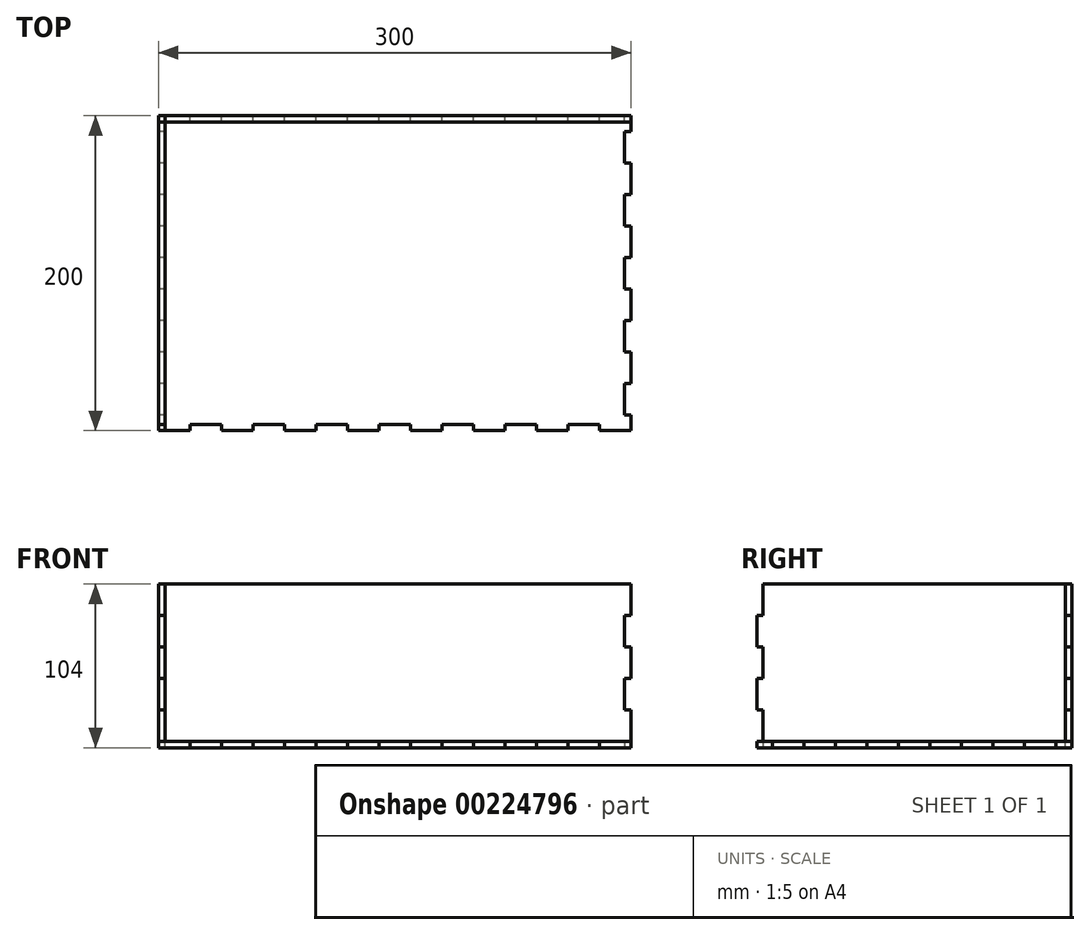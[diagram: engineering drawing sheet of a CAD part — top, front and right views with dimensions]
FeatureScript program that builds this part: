
annotation { "Feature Type Name" : "Feature", "Feature Type Description" : "" }
export const myFeature = defineFeature(function(context is Context, id is Id, definition is map)
    precondition{}
    {
        {
            var Q0;
            Q0=qCreatedBy(makeId("Top.planeOp"),FACE);
            var sketch = newSketch(context, id + "F0", { "sketchPlane" : qUnion([Q0])});
            skLineSegment(sketch, "E0.bottom", {"start": v(150, 100) * mm, "end": v(130, 100) * mm});
            skLineSegment(sketch, "E0.top", {"start": v(150, -100) * mm, "end": v(130, -100) * mm});
            skLineSegment(sketch, "E0.left", {"start": v(150, 100) * mm, "end": v(150, 90) * mm});
            skLineSegment(sketch, "E0.right", {"start": v(-150, 100) * mm, "end": v(-150, 90) * mm});
            skPoint(sketch, "E0.middle", {"position": v(0, 0) * mm});
            skPoint(sketch, "E1.endSnap0", {"position": v(0, 100) * mm});
            skLineSegment(sketch, "E2", {"start": v(0, 96) * mm, "end": v(10, 96) * mm});
            skLineSegment(sketch, "E3", {"start": v(10, 96) * mm, "end": v(10, 100) * mm});
            skLineSegment(sketch, "E4.MirrorCS", {"start": v(-10, 96) * mm, "end": v(-10, 100) * mm});
            skLineSegment(sketch, "E5.MirrorCS", {"start": v(0, 96) * mm, "end": v(-10, 96) * mm});
            skPoint(sketch, "E1.start.orphan", {"position": v(0, 100) * mm});
            skLineSegment(sketch, "E6.1.0.0", {"start": v(30, 96) * mm, "end": v(30, 100) * mm});
            skLineSegment(sketch, "E6.1.0.1", {"start": v(40, 96) * mm, "end": v(30, 96) * mm});
            skLineSegment(sketch, "E6.1.0.2", {"start": v(40, 96) * mm, "end": v(50, 96) * mm});
            skLineSegment(sketch, "E6.1.0.3", {"start": v(50, 96) * mm, "end": v(50, 100) * mm});
            skLineSegment(sketch, "E6.2.0.0", {"start": v(70, 96) * mm, "end": v(70, 100) * mm});
            skLineSegment(sketch, "E6.2.0.1", {"start": v(80, 96) * mm, "end": v(70, 96) * mm});
            skLineSegment(sketch, "E6.2.0.2", {"start": v(80, 96) * mm, "end": v(90, 96) * mm});
            skLineSegment(sketch, "E6.2.0.3", {"start": v(90, 96) * mm, "end": v(90, 100) * mm});
            skLineSegment(sketch, "E6.3.0.0", {"start": v(110, 96) * mm, "end": v(110, 100) * mm});
            skLineSegment(sketch, "E6.3.0.1", {"start": v(120, 96) * mm, "end": v(110, 96) * mm});
            skLineSegment(sketch, "E6.3.0.2", {"start": v(120, 96) * mm, "end": v(130, 96) * mm});
            skLineSegment(sketch, "E6.3.0.3", {"start": v(130, 96) * mm, "end": v(130, 100) * mm});
            skLineSegment(sketch, "E6.direction1", {"start": v(-10, 96) * mm, "end": v(30, 96) * mm, "construction": true});
            skLineSegment(sketch, "E7.MirrorCS", {"start": v(-110, 96) * mm, "end": v(-110, 100) * mm});
            skLineSegment(sketch, "E8.MirrorCS", {"start": v(-70, 96) * mm, "end": v(-70, 100) * mm});
            skLineSegment(sketch, "E9.MirrorCS", {"start": v(-50, 96) * mm, "end": v(-50, 100) * mm});
            skLineSegment(sketch, "E10.MirrorCS", {"start": v(-30, 96) * mm, "end": v(-30, 100) * mm});
            skLineSegment(sketch, "E11.MirrorCS", {"start": v(-90, 96) * mm, "end": v(-90, 100) * mm});
            skLineSegment(sketch, "E12.MirrorCS", {"start": v(-130, 96) * mm, "end": v(-130, 100) * mm});
            skLineSegment(sketch, "E13.MirrorCS", {"start": v(-120, 96) * mm, "end": v(-130, 96) * mm});
            skLineSegment(sketch, "E14.MirrorCS", {"start": v(10, 96) * mm, "end": v(-30, 96) * mm, "construction": true});
            skLineSegment(sketch, "E15.MirrorCS", {"start": v(-40, 96) * mm, "end": v(-50, 96) * mm});
            skLineSegment(sketch, "E16.MirrorCS", {"start": v(-40, 96) * mm, "end": v(-30, 96) * mm});
            skLineSegment(sketch, "E17.MirrorCS", {"start": v(-80, 96) * mm, "end": v(-90, 96) * mm});
            skLineSegment(sketch, "E18.MirrorCS", {"start": v(-120, 96) * mm, "end": v(-110, 96) * mm});
            skLineSegment(sketch, "E19.MirrorCS", {"start": v(-80, 96) * mm, "end": v(-70, 96) * mm});
            skPoint(sketch, "E20.MirrorP", {"position": v(0, -100) * mm});
            skLineSegment(sketch, "E21.MirrorCS", {"start": v(-10, -96) * mm, "end": v(-10, -100) * mm});
            skLineSegment(sketch, "E22.MirrorCS", {"start": v(10, -96) * mm, "end": v(10, -100) * mm});
            skLineSegment(sketch, "E23.MirrorCS", {"start": v(0, -96) * mm, "end": v(10, -96) * mm});
            skLineSegment(sketch, "E24.MirrorCS", {"start": v(0, -96) * mm, "end": v(-10, -96) * mm});
            skLineSegment(sketch, "E25.MirrorCS", {"start": v(-70, -96) * mm, "end": v(-70, -100) * mm});
            skLineSegment(sketch, "E26.MirrorCS", {"start": v(-130, -96) * mm, "end": v(-130, -100) * mm});
            skLineSegment(sketch, "E27.MirrorCS", {"start": v(-110, -96) * mm, "end": v(-110, -100) * mm});
            skLineSegment(sketch, "E28.MirrorCS", {"start": v(-30, -96) * mm, "end": v(-30, -100) * mm});
            skLineSegment(sketch, "E29.MirrorCS", {"start": v(110, -96) * mm, "end": v(110, -100) * mm});
            skLineSegment(sketch, "E30.MirrorCS", {"start": v(30, -96) * mm, "end": v(30, -100) * mm});
            skLineSegment(sketch, "E31.MirrorCS", {"start": v(130, -96) * mm, "end": v(130, -100) * mm});
            skLineSegment(sketch, "E32.MirrorCS", {"start": v(-50, -96) * mm, "end": v(-50, -100) * mm});
            skLineSegment(sketch, "E33.MirrorCS", {"start": v(90, -96) * mm, "end": v(90, -100) * mm});
            skLineSegment(sketch, "E34.MirrorCS", {"start": v(-90, -96) * mm, "end": v(-90, -100) * mm});
            skLineSegment(sketch, "E35.MirrorCS", {"start": v(70, -96) * mm, "end": v(70, -100) * mm});
            skLineSegment(sketch, "E36.MirrorCS", {"start": v(50, -96) * mm, "end": v(50, -100) * mm});
            skLineSegment(sketch, "E37.MirrorCS", {"start": v(-40, -96) * mm, "end": v(-30, -96) * mm});
            skLineSegment(sketch, "E38.MirrorCS", {"start": v(120, -96) * mm, "end": v(130, -96) * mm});
            skLineSegment(sketch, "E39.MirrorCS", {"start": v(-120, -96) * mm, "end": v(-130, -96) * mm});
            skLineSegment(sketch, "E40.MirrorCS", {"start": v(-40, -96) * mm, "end": v(-50, -96) * mm});
            skLineSegment(sketch, "E41.MirrorCS", {"start": v(120, -96) * mm, "end": v(110, -96) * mm});
            skLineSegment(sketch, "E42.MirrorCS", {"start": v(-80, -96) * mm, "end": v(-70, -96) * mm});
            skLineSegment(sketch, "E43.MirrorCS", {"start": v(10, -96) * mm, "end": v(-30, -96) * mm, "construction": true});
            skLineSegment(sketch, "E44.MirrorCS", {"start": v(40, -96) * mm, "end": v(50, -96) * mm});
            skLineSegment(sketch, "E45.MirrorCS", {"start": v(40, -96) * mm, "end": v(30, -96) * mm});
            skLineSegment(sketch, "E46.MirrorCS", {"start": v(-80, -96) * mm, "end": v(-90, -96) * mm});
            skLineSegment(sketch, "E47.MirrorCS", {"start": v(-120, -96) * mm, "end": v(-110, -96) * mm});
            skLineSegment(sketch, "E48.MirrorCS", {"start": v(80, -96) * mm, "end": v(90, -96) * mm});
            skLineSegment(sketch, "E49.MirrorCS", {"start": v(80, -96) * mm, "end": v(70, -96) * mm});
            skLineSegment(sketch, "E50.MirrorCS", {"start": v(-10, -96) * mm, "end": v(30, -96) * mm, "construction": true});
            skPoint(sketch, "E51.endSnap0", {"position": v(-150, 0) * mm});
            skLineSegment(sketch, "E52", {"start": v(-146, 0) * mm, "end": v(-146, 10) * mm});
            skLineSegment(sketch, "E53", {"start": v(-146, 10) * mm, "end": v(-150, 10) * mm});
            skLineSegment(sketch, "E54.MirrorCS", {"start": v(-146, 0) * mm, "end": v(-146, -10) * mm});
            skLineSegment(sketch, "E55.MirrorCS", {"start": v(-146, -10) * mm, "end": v(-150, -10) * mm});
            skPoint(sketch, "E51.start.orphan", {"position": v(-150, 0) * mm});
            skLineSegment(sketch, "E56.0.1.0", {"start": v(-146, 30) * mm, "end": v(-150, 30) * mm});
            skLineSegment(sketch, "E56.0.1.1", {"start": v(-146, 40) * mm, "end": v(-146, 30) * mm});
            skLineSegment(sketch, "E56.0.1.2", {"start": v(-146, 40) * mm, "end": v(-146, 50) * mm});
            skLineSegment(sketch, "E56.0.1.3", {"start": v(-146, 50) * mm, "end": v(-150, 50) * mm});
            skLineSegment(sketch, "E56.0.2.0", {"start": v(-146, 70) * mm, "end": v(-150, 70) * mm});
            skLineSegment(sketch, "E56.0.2.1", {"start": v(-146, 80) * mm, "end": v(-146, 70) * mm});
            skLineSegment(sketch, "E56.0.2.2", {"start": v(-146, 80) * mm, "end": v(-146, 90) * mm});
            skLineSegment(sketch, "E56.0.2.3", {"start": v(-146, 90) * mm, "end": v(-150, 90) * mm});
            skLineSegment(sketch, "E56.direction1", {"start": v(-150, -10) * mm, "end": v(-125, -10) * mm, "construction": true});
            skLineSegment(sketch, "E56.direction2", {"start": v(-150, 10) * mm, "end": v(-150, 30) * mm, "construction": true});
            skLineSegment(sketch, "E57.MirrorCS", {"start": v(-146, -30) * mm, "end": v(-150, -30) * mm});
            skLineSegment(sketch, "E58.MirrorCS", {"start": v(-146, -90) * mm, "end": v(-150, -90) * mm});
            skLineSegment(sketch, "E59.MirrorCS", {"start": v(-146, -70) * mm, "end": v(-150, -70) * mm});
            skLineSegment(sketch, "E60.MirrorCS", {"start": v(-146, -50) * mm, "end": v(-150, -50) * mm});
            skLineSegment(sketch, "E61.MirrorCS", {"start": v(-146, -80) * mm, "end": v(-146, -90) * mm});
            skLineSegment(sketch, "E62.MirrorCS", {"start": v(-146, -80) * mm, "end": v(-146, -70) * mm});
            skLineSegment(sketch, "E63.MirrorCS", {"start": v(-146, -40) * mm, "end": v(-146, -30) * mm});
            skLineSegment(sketch, "E64.MirrorCS", {"start": v(-146, -40) * mm, "end": v(-146, -50) * mm});
            skLineSegment(sketch, "E65.MirrorCS", {"start": v(-150, -10) * mm, "end": v(-150, -30) * mm, "construction": true});
            skLineSegment(sketch, "E66.MirrorCS", {"start": v(146, -10) * mm, "end": v(150, -10) * mm});
            skLineSegment(sketch, "E67.MirrorCS", {"start": v(146, 10) * mm, "end": v(150, 10) * mm});
            skPoint(sketch, "E68.MirrorP", {"position": v(150, 0) * mm});
            skLineSegment(sketch, "E69.MirrorCS", {"start": v(146, -30) * mm, "end": v(150, -30) * mm});
            skLineSegment(sketch, "E70.MirrorCS", {"start": v(146, 30) * mm, "end": v(150, 30) * mm});
            skLineSegment(sketch, "E71.MirrorCS", {"start": v(146, -90) * mm, "end": v(150, -90) * mm});
            skLineSegment(sketch, "E72.MirrorCS", {"start": v(146, -70) * mm, "end": v(150, -70) * mm});
            skLineSegment(sketch, "E73.MirrorCS", {"start": v(146, 0) * mm, "end": v(146, -10) * mm});
            skLineSegment(sketch, "E74.MirrorCS", {"start": v(146, 90) * mm, "end": v(150, 90) * mm});
            skLineSegment(sketch, "E75.MirrorCS", {"start": v(146, 70) * mm, "end": v(150, 70) * mm});
            skLineSegment(sketch, "E76.MirrorCS", {"start": v(146, -50) * mm, "end": v(150, -50) * mm});
            skLineSegment(sketch, "E77.MirrorCS", {"start": v(146, 0) * mm, "end": v(146, 10) * mm});
            skLineSegment(sketch, "E78.MirrorCS", {"start": v(146, 50) * mm, "end": v(150, 50) * mm});
            skLineSegment(sketch, "E79.MirrorCS", {"start": v(146, 80) * mm, "end": v(146, 90) * mm});
            skLineSegment(sketch, "E80.MirrorCS", {"start": v(146, 80) * mm, "end": v(146, 70) * mm});
            skLineSegment(sketch, "E81.MirrorCS", {"start": v(146, -40) * mm, "end": v(146, -50) * mm});
            skLineSegment(sketch, "E82.MirrorCS", {"start": v(146, -40) * mm, "end": v(146, -30) * mm});
            skLineSegment(sketch, "E83.MirrorCS", {"start": v(146, 40) * mm, "end": v(146, 50) * mm});
            skLineSegment(sketch, "E84.MirrorCS", {"start": v(150, 10) * mm, "end": v(150, 30) * mm, "construction": true});
            skLineSegment(sketch, "E85.MirrorCS", {"start": v(146, 40) * mm, "end": v(146, 30) * mm});
            skLineSegment(sketch, "E86.MirrorCS", {"start": v(146, -80) * mm, "end": v(146, -70) * mm});
            skLineSegment(sketch, "E87.MirrorCS", {"start": v(146, -80) * mm, "end": v(146, -90) * mm});
            skLineSegment(sketch, "E88.trimOffspring", {"start": v(-130, 100) * mm, "end": v(-150, 100) * mm});
            skLineSegment(sketch, "E89.trimOffspring", {"start": v(-90, 100) * mm, "end": v(-110, 100) * mm});
            skLineSegment(sketch, "E90.trimOffspring", {"start": v(-50, 100) * mm, "end": v(-70, 100) * mm});
            skLineSegment(sketch, "E91.trimOffspring", {"start": v(-10, 100) * mm, "end": v(-30, 100) * mm});
            skLineSegment(sketch, "E92.trimOffspring", {"start": v(30, 100) * mm, "end": v(10, 100) * mm});
            skLineSegment(sketch, "E93.trimOffspring", {"start": v(70, 100) * mm, "end": v(50, 100) * mm});
            skLineSegment(sketch, "E94.trimOffspring", {"start": v(110, 100) * mm, "end": v(90, 100) * mm});
            skLineSegment(sketch, "E95.trimOffspring", {"start": v(-150, 70) * mm, "end": v(-150, 50) * mm});
            skLineSegment(sketch, "E96.trimOffspring", {"start": v(-150, 30) * mm, "end": v(-150, 10) * mm});
            skLineSegment(sketch, "E97.trimOffspring", {"start": v(-150, -50) * mm, "end": v(-150, -70) * mm});
            skLineSegment(sketch, "E98.trimOffspring", {"start": v(-150, -90) * mm, "end": v(-150, -100) * mm});
            skLineSegment(sketch, "E99.trimOffspring", {"start": v(-130, -100) * mm, "end": v(-150, -100) * mm});
            skLineSegment(sketch, "E100.trimOffspring", {"start": v(-90, -100) * mm, "end": v(-110, -100) * mm});
            skLineSegment(sketch, "E101.trimOffspring", {"start": v(-50, -100) * mm, "end": v(-70, -100) * mm});
            skLineSegment(sketch, "E102.trimOffspring", {"start": v(-10, -100) * mm, "end": v(-30, -100) * mm});
            skLineSegment(sketch, "E103.trimOffspring", {"start": v(30, -100) * mm, "end": v(10, -100) * mm});
            skLineSegment(sketch, "E104.trimOffspring", {"start": v(70, -100) * mm, "end": v(50, -100) * mm});
            skLineSegment(sketch, "E105.trimOffspring", {"start": v(110, -100) * mm, "end": v(90, -100) * mm});
            skLineSegment(sketch, "E106.trimOffspring", {"start": v(150, -90) * mm, "end": v(150, -100) * mm});
            skLineSegment(sketch, "E107.trimOffspring", {"start": v(150, -50) * mm, "end": v(150, -70) * mm});
            skLineSegment(sketch, "E108.trimOffspring", {"start": v(150, -10) * mm, "end": v(150, -30) * mm, "construction": true});
            skLineSegment(sketch, "E109.trimOffspring", {"start": v(150, 30) * mm, "end": v(150, 10) * mm});
            skLineSegment(sketch, "E110.trimOffspring", {"start": v(150, 70) * mm, "end": v(150, 50) * mm});
            skLineSegment(sketch, "E111.trimOffspring", {"start": v(150, -10) * mm, "end": v(150, -30) * mm});
            skLineSegment(sketch, "E112.trimOffspring", {"start": v(-150, -10) * mm, "end": v(-150, -30) * mm});
            skSolve(sketch);
        }
        {
            var Q0;
            Q0 = qSketchRegion(id + "F0", true);
            extrude(context, id + "F1", {"entities" : qUnion([Q0]), "depth" : 4 * mm});
        }
        {
            var Q0;
            Q0=makeQuery(id+"F1.opExtrude","CAP_FACE",FACE,{"disambiguationData":[OSD([sQuery(id+"F0.wireOp",EDGE,"E0.bottom"),sQuery(id+"F0.wireOp",EDGE,"E0.top"),sQuery(id+"F0.wireOp",EDGE,"E0.left"),sQuery(id+"F0.wireOp",EDGE,"E0.right"),sQuery(id+"F0.wireOp",EDGE,"E6.1.0.0"),sQuery(id+"F0.wireOp",EDGE,"E6.1.0.1"),sQuery(id+"F0.wireOp",EDGE,"E6.1.0.2"),sQuery(id+"F0.wireOp",EDGE,"E6.1.0.3"),sQuery(id+"F0.wireOp",EDGE,"E6.2.0.0"),sQuery(id+"F0.wireOp",EDGE,"E6.2.0.1"),sQuery(id+"F0.wireOp",EDGE,"E6.2.0.2"),sQuery(id+"F0.wireOp",EDGE,"E6.2.0.3"),sQuery(id+"F0.wireOp",EDGE,"E6.3.0.0"),sQuery(id+"F0.wireOp",EDGE,"E6.3.0.1"),sQuery(id+"F0.wireOp",EDGE,"E6.3.0.2"),sQuery(id+"F0.wireOp",EDGE,"E6.3.0.3"),sQuery(id+"F0.wireOp",EDGE,"E7.MirrorCS"),sQuery(id+"F0.wireOp",EDGE,"E8.MirrorCS"),sQuery(id+"F0.wireOp",EDGE,"E9.MirrorCS"),sQuery(id+"F0.wireOp",EDGE,"E10.MirrorCS"),sQuery(id+"F0.wireOp",EDGE,"E2"),sQuery(id+"F0.wireOp",EDGE,"E3"),sQuery(id+"F0.wireOp",EDGE,"E4.MirrorCS"),sQuery(id+"F0.wireOp",EDGE,"E5.MirrorCS"),sQuery(id+"F0.wireOp",EDGE,"E11.MirrorCS"),sQuery(id+"F0.wireOp",EDGE,"E12.MirrorCS"),sQuery(id+"F0.wireOp",EDGE,"E13.MirrorCS"),sQuery(id+"F0.wireOp",EDGE,"E15.MirrorCS"),sQuery(id+"F0.wireOp",EDGE,"E16.MirrorCS"),sQuery(id+"F0.wireOp",EDGE,"E17.MirrorCS"),sQuery(id+"F0.wireOp",EDGE,"E18.MirrorCS"),sQuery(id+"F0.wireOp",EDGE,"E19.MirrorCS"),sQuery(id+"F0.wireOp",EDGE,"E22.MirrorCS"),sQuery(id+"F0.wireOp",EDGE,"E21.MirrorCS"),sQuery(id+"F0.wireOp",EDGE,"E25.MirrorCS"),sQuery(id+"F0.wireOp",EDGE,"E23.MirrorCS"),sQuery(id+"F0.wireOp",EDGE,"E26.MirrorCS"),sQuery(id+"F0.wireOp",EDGE,"E27.MirrorCS"),sQuery(id+"F0.wireOp",EDGE,"E28.MirrorCS"),sQuery(id+"F0.wireOp",EDGE,"E24.MirrorCS"),sQuery(id+"F0.wireOp",EDGE,"E29.MirrorCS"),sQuery(id+"F0.wireOp",EDGE,"E30.MirrorCS"),sQuery(id+"F0.wireOp",EDGE,"E31.MirrorCS"),sQuery(id+"F0.wireOp",EDGE,"E32.MirrorCS"),sQuery(id+"F0.wireOp",EDGE,"E33.MirrorCS"),sQuery(id+"F0.wireOp",EDGE,"E34.MirrorCS"),sQuery(id+"F0.wireOp",EDGE,"E35.MirrorCS"),sQuery(id+"F0.wireOp",EDGE,"E36.MirrorCS"),sQuery(id+"F0.wireOp",EDGE,"E37.MirrorCS"),sQuery(id+"F0.wireOp",EDGE,"E38.MirrorCS"),sQuery(id+"F0.wireOp",EDGE,"E39.MirrorCS"),sQuery(id+"F0.wireOp",EDGE,"E40.MirrorCS"),sQuery(id+"F0.wireOp",EDGE,"E41.MirrorCS"),sQuery(id+"F0.wireOp",EDGE,"E42.MirrorCS"),sQuery(id+"F0.wireOp",EDGE,"E44.MirrorCS"),sQuery(id+"F0.wireOp",EDGE,"E45.MirrorCS"),sQuery(id+"F0.wireOp",EDGE,"E46.MirrorCS"),sQuery(id+"F0.wireOp",EDGE,"E47.MirrorCS"),sQuery(id+"F0.wireOp",EDGE,"E48.MirrorCS"),sQuery(id+"F0.wireOp",EDGE,"E49.MirrorCS"),sQuery(id+"F0.wireOp",EDGE,"E56.0.1.0"),sQuery(id+"F0.wireOp",EDGE,"E56.0.1.1"),sQuery(id+"F0.wireOp",EDGE,"E56.0.1.2"),sQuery(id+"F0.wireOp",EDGE,"E56.0.1.3"),sQuery(id+"F0.wireOp",EDGE,"E56.0.2.0"),sQuery(id+"F0.wireOp",EDGE,"E56.0.2.1"),sQuery(id+"F0.wireOp",EDGE,"E56.0.2.2"),sQuery(id+"F0.wireOp",EDGE,"E56.0.2.3"),sQuery(id+"F0.wireOp",EDGE,"E53"),sQuery(id+"F0.wireOp",EDGE,"E57.MirrorCS"),sQuery(id+"F0.wireOp",EDGE,"E55.MirrorCS"),sQuery(id+"F0.wireOp",EDGE,"E58.MirrorCS"),sQuery(id+"F0.wireOp",EDGE,"E59.MirrorCS"),sQuery(id+"F0.wireOp",EDGE,"E60.MirrorCS"),sQuery(id+"F0.wireOp",EDGE,"E61.MirrorCS"),sQuery(id+"F0.wireOp",EDGE,"E62.MirrorCS"),sQuery(id+"F0.wireOp",EDGE,"E52"),sQuery(id+"F0.wireOp",EDGE,"E63.MirrorCS"),sQuery(id+"F0.wireOp",EDGE,"E64.MirrorCS"),sQuery(id+"F0.wireOp",EDGE,"E54.MirrorCS"),sQuery(id+"F0.wireOp",EDGE,"E66.MirrorCS"),sQuery(id+"F0.wireOp",EDGE,"E67.MirrorCS"),sQuery(id+"F0.wireOp",EDGE,"E69.MirrorCS"),sQuery(id+"F0.wireOp",EDGE,"E70.MirrorCS"),sQuery(id+"F0.wireOp",EDGE,"E71.MirrorCS"),sQuery(id+"F0.wireOp",EDGE,"E72.MirrorCS"),sQuery(id+"F0.wireOp",EDGE,"E74.MirrorCS"),sQuery(id+"F0.wireOp",EDGE,"E75.MirrorCS"),sQuery(id+"F0.wireOp",EDGE,"E76.MirrorCS"),sQuery(id+"F0.wireOp",EDGE,"E78.MirrorCS"),sQuery(id+"F0.wireOp",EDGE,"E73.MirrorCS"),sQuery(id+"F0.wireOp",EDGE,"E79.MirrorCS"),sQuery(id+"F0.wireOp",EDGE,"E80.MirrorCS"),sQuery(id+"F0.wireOp",EDGE,"E77.MirrorCS"),sQuery(id+"F0.wireOp",EDGE,"E81.MirrorCS"),sQuery(id+"F0.wireOp",EDGE,"E82.MirrorCS"),sQuery(id+"F0.wireOp",EDGE,"E83.MirrorCS"),sQuery(id+"F0.wireOp",EDGE,"E85.MirrorCS"),sQuery(id+"F0.wireOp",EDGE,"E86.MirrorCS"),sQuery(id+"F0.wireOp",EDGE,"E87.MirrorCS"),sQuery(id+"F0.wireOp",EDGE,"E88.trimOffspring"),sQuery(id+"F0.wireOp",EDGE,"E89.trimOffspring"),sQuery(id+"F0.wireOp",EDGE,"E90.trimOffspring"),sQuery(id+"F0.wireOp",EDGE,"E91.trimOffspring"),sQuery(id+"F0.wireOp",EDGE,"E92.trimOffspring"),sQuery(id+"F0.wireOp",EDGE,"E93.trimOffspring"),sQuery(id+"F0.wireOp",EDGE,"E94.trimOffspring"),sQuery(id+"F0.wireOp",EDGE,"E95.trimOffspring"),sQuery(id+"F0.wireOp",EDGE,"E96.trimOffspring"),sQuery(id+"F0.wireOp",EDGE,"E97.trimOffspring"),sQuery(id+"F0.wireOp",EDGE,"E98.trimOffspring"),sQuery(id+"F0.wireOp",EDGE,"E99.trimOffspring"),sQuery(id+"F0.wireOp",EDGE,"E100.trimOffspring"),sQuery(id+"F0.wireOp",EDGE,"E101.trimOffspring"),sQuery(id+"F0.wireOp",EDGE,"E102.trimOffspring"),sQuery(id+"F0.wireOp",EDGE,"E103.trimOffspring"),sQuery(id+"F0.wireOp",EDGE,"E104.trimOffspring"),sQuery(id+"F0.wireOp",EDGE,"E105.trimOffspring"),sQuery(id+"F0.wireOp",EDGE,"E106.trimOffspring"),sQuery(id+"F0.wireOp",EDGE,"E107.trimOffspring"),sQuery(id+"F0.wireOp",EDGE,"E109.trimOffspring"),sQuery(id+"F0.wireOp",EDGE,"E110.trimOffspring"),sQuery(id+"F0.wireOp",EDGE,"E111.trimOffspring"),sQuery(id+"F0.wireOp",EDGE,"E112.trimOffspring")])],"isStart":false});
            var sketch = newSketch(context, id + "F2", { "sketchPlane" : qUnion([Q0])});
            skLineSegment(sketch, "E113.0", {"start": v(150, 100) * mm, "end": v(130, 100) * mm});
            skLineSegment(sketch, "E113.1", {"start": v(-90, 96) * mm, "end": v(-90, 100) * mm});
            skLineSegment(sketch, "E113.2", {"start": v(-50, 100) * mm, "end": v(-70, 100) * mm});
            skLineSegment(sketch, "E113.3", {"start": v(-10, 100) * mm, "end": v(-30, 100) * mm});
            skLineSegment(sketch, "E113.4", {"start": v(70, 96) * mm, "end": v(90, 96) * mm});
            skLineSegment(sketch, "E113.6", {"start": v(70, 96) * mm, "end": v(70, 100) * mm});
            skLineSegment(sketch, "E113.7", {"start": v(-50, 96) * mm, "end": v(-50, 100) * mm});
            skLineSegment(sketch, "E113.8", {"start": v(-10, 96) * mm, "end": v(10, 96) * mm});
            skLineSegment(sketch, "E113.9", {"start": v(-130, 96) * mm, "end": v(-130, 100) * mm});
            skLineSegment(sketch, "E113.10", {"start": v(-130, 96) * mm, "end": v(-110, 96) * mm});
            skLineSegment(sketch, "E113.11", {"start": v(-90, 96) * mm, "end": v(-70, 96) * mm});
            skLineSegment(sketch, "E113.13", {"start": v(30, 96) * mm, "end": v(30, 100) * mm});
            skLineSegment(sketch, "E113.15", {"start": v(-130, 100) * mm, "end": v(-150, 100) * mm});
            skLineSegment(sketch, "E113.17", {"start": v(70, 100) * mm, "end": v(50, 100) * mm});
            skLineSegment(sketch, "E113.18", {"start": v(-70, 96) * mm, "end": v(-70, 100) * mm});
            skLineSegment(sketch, "E113.19", {"start": v(50, 96) * mm, "end": v(50, 100) * mm});
            skLineSegment(sketch, "E113.20", {"start": v(-110, 96) * mm, "end": v(-110, 100) * mm});
            skLineSegment(sketch, "E113.21", {"start": v(-50, 96) * mm, "end": v(-30, 96) * mm});
            skLineSegment(sketch, "E113.22", {"start": v(90, 96) * mm, "end": v(90, 100) * mm});
            skLineSegment(sketch, "E113.23", {"start": v(30, 100) * mm, "end": v(10, 100) * mm});
            skLineSegment(sketch, "E113.24", {"start": v(-30, 96) * mm, "end": v(-30, 100) * mm});
            skLineSegment(sketch, "E113.26", {"start": v(130, 96) * mm, "end": v(130, 100) * mm});
            skLineSegment(sketch, "E113.29", {"start": v(30, 96) * mm, "end": v(50, 96) * mm});
            skLineSegment(sketch, "E113.30", {"start": v(-90, 100) * mm, "end": v(-110, 100) * mm});
            skLineSegment(sketch, "E113.32", {"start": v(110, 96) * mm, "end": v(110, 100) * mm});
            skLineSegment(sketch, "E113.33", {"start": v(10, 96) * mm, "end": v(10, 100) * mm});
            skLineSegment(sketch, "E113.34", {"start": v(110, 100) * mm, "end": v(90, 100) * mm});
            skLineSegment(sketch, "E113.35", {"start": v(110, 96) * mm, "end": v(130, 96) * mm});
            skLineSegment(sketch, "E113.36", {"start": v(-10, 96) * mm, "end": v(-10, 100) * mm});
            skLineSegment(sketch, "E113.37", {"start": v(-90, 96) * mm, "end": v(-70, 96) * mm});
            skLineSegment(sketch, "E113.38", {"start": v(70, 96) * mm, "end": v(90, 96) * mm});
            skLineSegment(sketch, "E113.40", {"start": v(30, 100) * mm, "end": v(10, 100) * mm});
            skLineSegment(sketch, "E113.42", {"start": v(-50, 96) * mm, "end": v(-50, 100) * mm});
            skLineSegment(sketch, "E113.44", {"start": v(70, 100) * mm, "end": v(50, 100) * mm});
            skLineSegment(sketch, "E113.46", {"start": v(-130, 96) * mm, "end": v(-130, 100) * mm});
            skLineSegment(sketch, "E113.47", {"start": v(30, 96) * mm, "end": v(50, 96) * mm});
            skLineSegment(sketch, "E113.49", {"start": v(-110, 96) * mm, "end": v(-110, 100) * mm});
            skLineSegment(sketch, "E113.53", {"start": v(-90, 100) * mm, "end": v(-110, 100) * mm});
            skLineSegment(sketch, "E113.54", {"start": v(-70, 96) * mm, "end": v(-70, 100) * mm});
            skLineSegment(sketch, "E113.55", {"start": v(110, 96) * mm, "end": v(110, 100) * mm});
            skLineSegment(sketch, "E113.56", {"start": v(10, 96) * mm, "end": v(10, 100) * mm});
            skLineSegment(sketch, "E113.57", {"start": v(50, 96) * mm, "end": v(50, 100) * mm});
            skLineSegment(sketch, "E113.59", {"start": v(-50, 100) * mm, "end": v(-70, 100) * mm});
            skLineSegment(sketch, "E113.62", {"start": v(-50, 96) * mm, "end": v(-30, 96) * mm});
            skLineSegment(sketch, "E113.63", {"start": v(70, 96) * mm, "end": v(70, 100) * mm});
            skLineSegment(sketch, "E113.64", {"start": v(-10, 100) * mm, "end": v(-30, 100) * mm});
            skLineSegment(sketch, "E113.66", {"start": v(150, 100) * mm, "end": v(130, 100) * mm});
            skLineSegment(sketch, "E113.67", {"start": v(-30, 96) * mm, "end": v(-30, 100) * mm});
            skLineSegment(sketch, "E113.69", {"start": v(90, 96) * mm, "end": v(90, 100) * mm});
            skLineSegment(sketch, "E113.70", {"start": v(-10, 96) * mm, "end": v(10, 96) * mm});
            skLineSegment(sketch, "E113.71", {"start": v(110, 100) * mm, "end": v(90, 100) * mm});
            skLineSegment(sketch, "E113.76", {"start": v(-130, 96) * mm, "end": v(-110, 96) * mm});
            skLineSegment(sketch, "E113.79", {"start": v(110, 96) * mm, "end": v(130, 96) * mm});
            skLineSegment(sketch, "E113.80", {"start": v(-10, 96) * mm, "end": v(-10, 100) * mm});
            skLineSegment(sketch, "E113.83", {"start": v(30, 96) * mm, "end": v(30, 100) * mm});
            skLineSegment(sketch, "E113.84", {"start": v(130, 96) * mm, "end": v(130, 100) * mm});
            skLineSegment(sketch, "E113.85", {"start": v(-90, 96) * mm, "end": v(-90, 100) * mm});
            skLineSegment(sketch, "E113.86", {"start": v(-130, 100) * mm, "end": v(-150, 100) * mm});
            skLineSegment(sketch, "E114", {"start": v(-150, 100) * mm, "end": v(150, 100) * mm});
            skSolve(sketch);
        }
        {
            var Q0;
            Q0 = qSketchRegion(id + "F2", true);
            var Q1;
            Q1=makeQuery(id+"F1.opExtrude","CAP_FACE",FACE,{"disambiguationData":[OSD([sQuery(id+"F0.wireOp",EDGE,"E0.bottom"),sQuery(id+"F0.wireOp",EDGE,"E0.top"),sQuery(id+"F0.wireOp",EDGE,"E0.left"),sQuery(id+"F0.wireOp",EDGE,"E0.right"),sQuery(id+"F0.wireOp",EDGE,"E6.1.0.0"),sQuery(id+"F0.wireOp",EDGE,"E6.1.0.1"),sQuery(id+"F0.wireOp",EDGE,"E6.1.0.2"),sQuery(id+"F0.wireOp",EDGE,"E6.1.0.3"),sQuery(id+"F0.wireOp",EDGE,"E6.2.0.0"),sQuery(id+"F0.wireOp",EDGE,"E6.2.0.1"),sQuery(id+"F0.wireOp",EDGE,"E6.2.0.2"),sQuery(id+"F0.wireOp",EDGE,"E6.2.0.3"),sQuery(id+"F0.wireOp",EDGE,"E6.3.0.0"),sQuery(id+"F0.wireOp",EDGE,"E6.3.0.1"),sQuery(id+"F0.wireOp",EDGE,"E6.3.0.2"),sQuery(id+"F0.wireOp",EDGE,"E6.3.0.3"),sQuery(id+"F0.wireOp",EDGE,"E7.MirrorCS"),sQuery(id+"F0.wireOp",EDGE,"E8.MirrorCS"),sQuery(id+"F0.wireOp",EDGE,"E9.MirrorCS"),sQuery(id+"F0.wireOp",EDGE,"E10.MirrorCS"),sQuery(id+"F0.wireOp",EDGE,"E2"),sQuery(id+"F0.wireOp",EDGE,"E3"),sQuery(id+"F0.wireOp",EDGE,"E4.MirrorCS"),sQuery(id+"F0.wireOp",EDGE,"E5.MirrorCS"),sQuery(id+"F0.wireOp",EDGE,"E11.MirrorCS"),sQuery(id+"F0.wireOp",EDGE,"E12.MirrorCS"),sQuery(id+"F0.wireOp",EDGE,"E13.MirrorCS"),sQuery(id+"F0.wireOp",EDGE,"E15.MirrorCS"),sQuery(id+"F0.wireOp",EDGE,"E16.MirrorCS"),sQuery(id+"F0.wireOp",EDGE,"E17.MirrorCS"),sQuery(id+"F0.wireOp",EDGE,"E18.MirrorCS"),sQuery(id+"F0.wireOp",EDGE,"E19.MirrorCS"),sQuery(id+"F0.wireOp",EDGE,"E22.MirrorCS"),sQuery(id+"F0.wireOp",EDGE,"E21.MirrorCS"),sQuery(id+"F0.wireOp",EDGE,"E25.MirrorCS"),sQuery(id+"F0.wireOp",EDGE,"E23.MirrorCS"),sQuery(id+"F0.wireOp",EDGE,"E26.MirrorCS"),sQuery(id+"F0.wireOp",EDGE,"E27.MirrorCS"),sQuery(id+"F0.wireOp",EDGE,"E28.MirrorCS"),sQuery(id+"F0.wireOp",EDGE,"E24.MirrorCS"),sQuery(id+"F0.wireOp",EDGE,"E29.MirrorCS"),sQuery(id+"F0.wireOp",EDGE,"E30.MirrorCS"),sQuery(id+"F0.wireOp",EDGE,"E31.MirrorCS"),sQuery(id+"F0.wireOp",EDGE,"E32.MirrorCS"),sQuery(id+"F0.wireOp",EDGE,"E33.MirrorCS"),sQuery(id+"F0.wireOp",EDGE,"E34.MirrorCS"),sQuery(id+"F0.wireOp",EDGE,"E35.MirrorCS"),sQuery(id+"F0.wireOp",EDGE,"E36.MirrorCS"),sQuery(id+"F0.wireOp",EDGE,"E37.MirrorCS"),sQuery(id+"F0.wireOp",EDGE,"E38.MirrorCS"),sQuery(id+"F0.wireOp",EDGE,"E39.MirrorCS"),sQuery(id+"F0.wireOp",EDGE,"E40.MirrorCS"),sQuery(id+"F0.wireOp",EDGE,"E41.MirrorCS"),sQuery(id+"F0.wireOp",EDGE,"E42.MirrorCS"),sQuery(id+"F0.wireOp",EDGE,"E44.MirrorCS"),sQuery(id+"F0.wireOp",EDGE,"E45.MirrorCS"),sQuery(id+"F0.wireOp",EDGE,"E46.MirrorCS"),sQuery(id+"F0.wireOp",EDGE,"E47.MirrorCS"),sQuery(id+"F0.wireOp",EDGE,"E48.MirrorCS"),sQuery(id+"F0.wireOp",EDGE,"E49.MirrorCS"),sQuery(id+"F0.wireOp",EDGE,"E56.0.1.0"),sQuery(id+"F0.wireOp",EDGE,"E56.0.1.1"),sQuery(id+"F0.wireOp",EDGE,"E56.0.1.2"),sQuery(id+"F0.wireOp",EDGE,"E56.0.1.3"),sQuery(id+"F0.wireOp",EDGE,"E56.0.2.0"),sQuery(id+"F0.wireOp",EDGE,"E56.0.2.1"),sQuery(id+"F0.wireOp",EDGE,"E56.0.2.2"),sQuery(id+"F0.wireOp",EDGE,"E56.0.2.3"),sQuery(id+"F0.wireOp",EDGE,"E53"),sQuery(id+"F0.wireOp",EDGE,"E57.MirrorCS"),sQuery(id+"F0.wireOp",EDGE,"E55.MirrorCS"),sQuery(id+"F0.wireOp",EDGE,"E58.MirrorCS"),sQuery(id+"F0.wireOp",EDGE,"E59.MirrorCS"),sQuery(id+"F0.wireOp",EDGE,"E60.MirrorCS"),sQuery(id+"F0.wireOp",EDGE,"E61.MirrorCS"),sQuery(id+"F0.wireOp",EDGE,"E62.MirrorCS"),sQuery(id+"F0.wireOp",EDGE,"E52"),sQuery(id+"F0.wireOp",EDGE,"E63.MirrorCS"),sQuery(id+"F0.wireOp",EDGE,"E64.MirrorCS"),sQuery(id+"F0.wireOp",EDGE,"E54.MirrorCS"),sQuery(id+"F0.wireOp",EDGE,"E66.MirrorCS"),sQuery(id+"F0.wireOp",EDGE,"E67.MirrorCS"),sQuery(id+"F0.wireOp",EDGE,"E69.MirrorCS"),sQuery(id+"F0.wireOp",EDGE,"E70.MirrorCS"),sQuery(id+"F0.wireOp",EDGE,"E71.MirrorCS"),sQuery(id+"F0.wireOp",EDGE,"E72.MirrorCS"),sQuery(id+"F0.wireOp",EDGE,"E74.MirrorCS"),sQuery(id+"F0.wireOp",EDGE,"E75.MirrorCS"),sQuery(id+"F0.wireOp",EDGE,"E76.MirrorCS"),sQuery(id+"F0.wireOp",EDGE,"E78.MirrorCS"),sQuery(id+"F0.wireOp",EDGE,"E73.MirrorCS"),sQuery(id+"F0.wireOp",EDGE,"E79.MirrorCS"),sQuery(id+"F0.wireOp",EDGE,"E80.MirrorCS"),sQuery(id+"F0.wireOp",EDGE,"E77.MirrorCS"),sQuery(id+"F0.wireOp",EDGE,"E81.MirrorCS"),sQuery(id+"F0.wireOp",EDGE,"E82.MirrorCS"),sQuery(id+"F0.wireOp",EDGE,"E83.MirrorCS"),sQuery(id+"F0.wireOp",EDGE,"E85.MirrorCS"),sQuery(id+"F0.wireOp",EDGE,"E86.MirrorCS"),sQuery(id+"F0.wireOp",EDGE,"E87.MirrorCS"),sQuery(id+"F0.wireOp",EDGE,"E88.trimOffspring"),sQuery(id+"F0.wireOp",EDGE,"E89.trimOffspring"),sQuery(id+"F0.wireOp",EDGE,"E90.trimOffspring"),sQuery(id+"F0.wireOp",EDGE,"E91.trimOffspring"),sQuery(id+"F0.wireOp",EDGE,"E92.trimOffspring"),sQuery(id+"F0.wireOp",EDGE,"E93.trimOffspring"),sQuery(id+"F0.wireOp",EDGE,"E94.trimOffspring"),sQuery(id+"F0.wireOp",EDGE,"E95.trimOffspring"),sQuery(id+"F0.wireOp",EDGE,"E96.trimOffspring"),sQuery(id+"F0.wireOp",EDGE,"E97.trimOffspring"),sQuery(id+"F0.wireOp",EDGE,"E98.trimOffspring"),sQuery(id+"F0.wireOp",EDGE,"E99.trimOffspring"),sQuery(id+"F0.wireOp",EDGE,"E100.trimOffspring"),sQuery(id+"F0.wireOp",EDGE,"E101.trimOffspring"),sQuery(id+"F0.wireOp",EDGE,"E102.trimOffspring"),sQuery(id+"F0.wireOp",EDGE,"E103.trimOffspring"),sQuery(id+"F0.wireOp",EDGE,"E104.trimOffspring"),sQuery(id+"F0.wireOp",EDGE,"E105.trimOffspring"),sQuery(id+"F0.wireOp",EDGE,"E106.trimOffspring"),sQuery(id+"F0.wireOp",EDGE,"E107.trimOffspring"),sQuery(id+"F0.wireOp",EDGE,"E109.trimOffspring"),sQuery(id+"F0.wireOp",EDGE,"E110.trimOffspring"),sQuery(id+"F0.wireOp",EDGE,"E111.trimOffspring"),sQuery(id+"F0.wireOp",EDGE,"E112.trimOffspring")])],"isStart":true});
            extrude(context, id + "F3", {"entities" : qUnion([Q0]), "endBound" : BoundingType.UP_TO_SURFACE, "oppositeDirection" : true, "endBoundEntityFace" : qUnion([Q1]), "depth" : 25 * mm});
        }
        {
            var Q0;
            Q0=makeQuery(id+"F1.opExtrude","CAP_FACE",FACE,{"disambiguationData":[OSD([sQuery(id+"F0.wireOp",EDGE,"E0.bottom"),sQuery(id+"F0.wireOp",EDGE,"E0.top"),sQuery(id+"F0.wireOp",EDGE,"E0.left"),sQuery(id+"F0.wireOp",EDGE,"E0.right"),sQuery(id+"F0.wireOp",EDGE,"E6.1.0.0"),sQuery(id+"F0.wireOp",EDGE,"E6.1.0.1"),sQuery(id+"F0.wireOp",EDGE,"E6.1.0.2"),sQuery(id+"F0.wireOp",EDGE,"E6.1.0.3"),sQuery(id+"F0.wireOp",EDGE,"E6.2.0.0"),sQuery(id+"F0.wireOp",EDGE,"E6.2.0.1"),sQuery(id+"F0.wireOp",EDGE,"E6.2.0.2"),sQuery(id+"F0.wireOp",EDGE,"E6.2.0.3"),sQuery(id+"F0.wireOp",EDGE,"E6.3.0.0"),sQuery(id+"F0.wireOp",EDGE,"E6.3.0.1"),sQuery(id+"F0.wireOp",EDGE,"E6.3.0.2"),sQuery(id+"F0.wireOp",EDGE,"E6.3.0.3"),sQuery(id+"F0.wireOp",EDGE,"E7.MirrorCS"),sQuery(id+"F0.wireOp",EDGE,"E8.MirrorCS"),sQuery(id+"F0.wireOp",EDGE,"E9.MirrorCS"),sQuery(id+"F0.wireOp",EDGE,"E10.MirrorCS"),sQuery(id+"F0.wireOp",EDGE,"E2"),sQuery(id+"F0.wireOp",EDGE,"E3"),sQuery(id+"F0.wireOp",EDGE,"E4.MirrorCS"),sQuery(id+"F0.wireOp",EDGE,"E5.MirrorCS"),sQuery(id+"F0.wireOp",EDGE,"E11.MirrorCS"),sQuery(id+"F0.wireOp",EDGE,"E12.MirrorCS"),sQuery(id+"F0.wireOp",EDGE,"E13.MirrorCS"),sQuery(id+"F0.wireOp",EDGE,"E15.MirrorCS"),sQuery(id+"F0.wireOp",EDGE,"E16.MirrorCS"),sQuery(id+"F0.wireOp",EDGE,"E17.MirrorCS"),sQuery(id+"F0.wireOp",EDGE,"E18.MirrorCS"),sQuery(id+"F0.wireOp",EDGE,"E19.MirrorCS"),sQuery(id+"F0.wireOp",EDGE,"E22.MirrorCS"),sQuery(id+"F0.wireOp",EDGE,"E21.MirrorCS"),sQuery(id+"F0.wireOp",EDGE,"E25.MirrorCS"),sQuery(id+"F0.wireOp",EDGE,"E23.MirrorCS"),sQuery(id+"F0.wireOp",EDGE,"E26.MirrorCS"),sQuery(id+"F0.wireOp",EDGE,"E27.MirrorCS"),sQuery(id+"F0.wireOp",EDGE,"E28.MirrorCS"),sQuery(id+"F0.wireOp",EDGE,"E24.MirrorCS"),sQuery(id+"F0.wireOp",EDGE,"E29.MirrorCS"),sQuery(id+"F0.wireOp",EDGE,"E30.MirrorCS"),sQuery(id+"F0.wireOp",EDGE,"E31.MirrorCS"),sQuery(id+"F0.wireOp",EDGE,"E32.MirrorCS"),sQuery(id+"F0.wireOp",EDGE,"E33.MirrorCS"),sQuery(id+"F0.wireOp",EDGE,"E34.MirrorCS"),sQuery(id+"F0.wireOp",EDGE,"E35.MirrorCS"),sQuery(id+"F0.wireOp",EDGE,"E36.MirrorCS"),sQuery(id+"F0.wireOp",EDGE,"E37.MirrorCS"),sQuery(id+"F0.wireOp",EDGE,"E38.MirrorCS"),sQuery(id+"F0.wireOp",EDGE,"E39.MirrorCS"),sQuery(id+"F0.wireOp",EDGE,"E40.MirrorCS"),sQuery(id+"F0.wireOp",EDGE,"E41.MirrorCS"),sQuery(id+"F0.wireOp",EDGE,"E42.MirrorCS"),sQuery(id+"F0.wireOp",EDGE,"E44.MirrorCS"),sQuery(id+"F0.wireOp",EDGE,"E45.MirrorCS"),sQuery(id+"F0.wireOp",EDGE,"E46.MirrorCS"),sQuery(id+"F0.wireOp",EDGE,"E47.MirrorCS"),sQuery(id+"F0.wireOp",EDGE,"E48.MirrorCS"),sQuery(id+"F0.wireOp",EDGE,"E49.MirrorCS"),sQuery(id+"F0.wireOp",EDGE,"E56.0.1.0"),sQuery(id+"F0.wireOp",EDGE,"E56.0.1.1"),sQuery(id+"F0.wireOp",EDGE,"E56.0.1.2"),sQuery(id+"F0.wireOp",EDGE,"E56.0.1.3"),sQuery(id+"F0.wireOp",EDGE,"E56.0.2.0"),sQuery(id+"F0.wireOp",EDGE,"E56.0.2.1"),sQuery(id+"F0.wireOp",EDGE,"E56.0.2.2"),sQuery(id+"F0.wireOp",EDGE,"E56.0.2.3"),sQuery(id+"F0.wireOp",EDGE,"E53"),sQuery(id+"F0.wireOp",EDGE,"E57.MirrorCS"),sQuery(id+"F0.wireOp",EDGE,"E55.MirrorCS"),sQuery(id+"F0.wireOp",EDGE,"E58.MirrorCS"),sQuery(id+"F0.wireOp",EDGE,"E59.MirrorCS"),sQuery(id+"F0.wireOp",EDGE,"E60.MirrorCS"),sQuery(id+"F0.wireOp",EDGE,"E61.MirrorCS"),sQuery(id+"F0.wireOp",EDGE,"E62.MirrorCS"),sQuery(id+"F0.wireOp",EDGE,"E52"),sQuery(id+"F0.wireOp",EDGE,"E63.MirrorCS"),sQuery(id+"F0.wireOp",EDGE,"E64.MirrorCS"),sQuery(id+"F0.wireOp",EDGE,"E54.MirrorCS"),sQuery(id+"F0.wireOp",EDGE,"E66.MirrorCS"),sQuery(id+"F0.wireOp",EDGE,"E67.MirrorCS"),sQuery(id+"F0.wireOp",EDGE,"E69.MirrorCS"),sQuery(id+"F0.wireOp",EDGE,"E70.MirrorCS"),sQuery(id+"F0.wireOp",EDGE,"E71.MirrorCS"),sQuery(id+"F0.wireOp",EDGE,"E72.MirrorCS"),sQuery(id+"F0.wireOp",EDGE,"E74.MirrorCS"),sQuery(id+"F0.wireOp",EDGE,"E75.MirrorCS"),sQuery(id+"F0.wireOp",EDGE,"E76.MirrorCS"),sQuery(id+"F0.wireOp",EDGE,"E78.MirrorCS"),sQuery(id+"F0.wireOp",EDGE,"E73.MirrorCS"),sQuery(id+"F0.wireOp",EDGE,"E79.MirrorCS"),sQuery(id+"F0.wireOp",EDGE,"E80.MirrorCS"),sQuery(id+"F0.wireOp",EDGE,"E77.MirrorCS"),sQuery(id+"F0.wireOp",EDGE,"E81.MirrorCS"),sQuery(id+"F0.wireOp",EDGE,"E82.MirrorCS"),sQuery(id+"F0.wireOp",EDGE,"E83.MirrorCS"),sQuery(id+"F0.wireOp",EDGE,"E85.MirrorCS"),sQuery(id+"F0.wireOp",EDGE,"E86.MirrorCS"),sQuery(id+"F0.wireOp",EDGE,"E87.MirrorCS"),sQuery(id+"F0.wireOp",EDGE,"E88.trimOffspring"),sQuery(id+"F0.wireOp",EDGE,"E89.trimOffspring"),sQuery(id+"F0.wireOp",EDGE,"E90.trimOffspring"),sQuery(id+"F0.wireOp",EDGE,"E91.trimOffspring"),sQuery(id+"F0.wireOp",EDGE,"E92.trimOffspring"),sQuery(id+"F0.wireOp",EDGE,"E93.trimOffspring"),sQuery(id+"F0.wireOp",EDGE,"E94.trimOffspring"),sQuery(id+"F0.wireOp",EDGE,"E95.trimOffspring"),sQuery(id+"F0.wireOp",EDGE,"E96.trimOffspring"),sQuery(id+"F0.wireOp",EDGE,"E97.trimOffspring"),sQuery(id+"F0.wireOp",EDGE,"E98.trimOffspring"),sQuery(id+"F0.wireOp",EDGE,"E99.trimOffspring"),sQuery(id+"F0.wireOp",EDGE,"E100.trimOffspring"),sQuery(id+"F0.wireOp",EDGE,"E101.trimOffspring"),sQuery(id+"F0.wireOp",EDGE,"E102.trimOffspring"),sQuery(id+"F0.wireOp",EDGE,"E103.trimOffspring"),sQuery(id+"F0.wireOp",EDGE,"E104.trimOffspring"),sQuery(id+"F0.wireOp",EDGE,"E105.trimOffspring"),sQuery(id+"F0.wireOp",EDGE,"E106.trimOffspring"),sQuery(id+"F0.wireOp",EDGE,"E107.trimOffspring"),sQuery(id+"F0.wireOp",EDGE,"E109.trimOffspring"),sQuery(id+"F0.wireOp",EDGE,"E110.trimOffspring"),sQuery(id+"F0.wireOp",EDGE,"E111.trimOffspring"),sQuery(id+"F0.wireOp",EDGE,"E112.trimOffspring")])],"isStart":false});
            var sketch = newSketch(context, id + "F4", { "sketchPlane" : qUnion([Q0])});
            skLineSegment(sketch, "E115.0", {"start": v(150, 100) * mm, "end": v(130, 100) * mm});
            skLineSegment(sketch, "E115.1", {"start": v(-50, 100) * mm, "end": v(-70, 100) * mm});
            skLineSegment(sketch, "E115.2", {"start": v(-10, 100) * mm, "end": v(-30, 100) * mm});
            skLineSegment(sketch, "E115.4", {"start": v(-130, 100) * mm, "end": v(-150, 100) * mm});
            skLineSegment(sketch, "E115.5", {"start": v(70, 100) * mm, "end": v(50, 100) * mm});
            skLineSegment(sketch, "E115.6", {"start": v(30, 100) * mm, "end": v(10, 100) * mm});
            skLineSegment(sketch, "E115.7", {"start": v(-90, 100) * mm, "end": v(-110, 100) * mm});
            skLineSegment(sketch, "E115.8", {"start": v(110, 100) * mm, "end": v(90, 100) * mm});
            skLineSegment(sketch, "E115.9", {"start": v(-10, 100) * mm, "end": v(10, 100) * mm});
            skLineSegment(sketch, "E115.10", {"start": v(110, 100) * mm, "end": v(130, 100) * mm});
            skLineSegment(sketch, "E115.11", {"start": v(30, 100) * mm, "end": v(50, 100) * mm});
            skLineSegment(sketch, "E115.12", {"start": v(-130, 100) * mm, "end": v(-110, 100) * mm});
            skLineSegment(sketch, "E115.13", {"start": v(-50, 100) * mm, "end": v(-30, 100) * mm});
            skLineSegment(sketch, "E115.14", {"start": v(70, 100) * mm, "end": v(90, 100) * mm});
            skLineSegment(sketch, "E115.15", {"start": v(-90, 100) * mm, "end": v(-70, 100) * mm});
            skLineSegment(sketch, "E115.17", {"start": v(-90, 96) * mm, "end": v(-90, 100) * mm});
            skLineSegment(sketch, "E115.18", {"start": v(30, 100) * mm, "end": v(10, 100) * mm});
            skLineSegment(sketch, "E115.19", {"start": v(70, 96) * mm, "end": v(90, 96) * mm});
            skLineSegment(sketch, "E115.21", {"start": v(70, 96) * mm, "end": v(70, 100) * mm});
            skLineSegment(sketch, "E115.22", {"start": v(70, 100) * mm, "end": v(50, 100) * mm});
            skLineSegment(sketch, "E115.23", {"start": v(-50, 96) * mm, "end": v(-50, 100) * mm});
            skLineSegment(sketch, "E115.24", {"start": v(-10, 96) * mm, "end": v(10, 96) * mm});
            skLineSegment(sketch, "E115.25", {"start": v(-130, 96) * mm, "end": v(-130, 100) * mm});
            skLineSegment(sketch, "E115.26", {"start": v(-130, 96) * mm, "end": v(-110, 96) * mm});
            skLineSegment(sketch, "E115.27", {"start": v(-90, 96) * mm, "end": v(-70, 96) * mm});
            skLineSegment(sketch, "E115.28", {"start": v(30, 96) * mm, "end": v(30, 100) * mm});
            skLineSegment(sketch, "E115.30", {"start": v(-90, 100) * mm, "end": v(-110, 100) * mm});
            skLineSegment(sketch, "E115.31", {"start": v(-50, 100) * mm, "end": v(-70, 100) * mm});
            skLineSegment(sketch, "E115.32", {"start": v(-70, 96) * mm, "end": v(-70, 100) * mm});
            skLineSegment(sketch, "E115.33", {"start": v(50, 96) * mm, "end": v(50, 100) * mm});
            skLineSegment(sketch, "E115.34", {"start": v(-110, 96) * mm, "end": v(-110, 100) * mm});
            skLineSegment(sketch, "E115.35", {"start": v(-10, 100) * mm, "end": v(-30, 100) * mm});
            skLineSegment(sketch, "E115.36", {"start": v(-50, 96) * mm, "end": v(-30, 96) * mm});
            skLineSegment(sketch, "E115.37", {"start": v(150, 100) * mm, "end": v(130, 100) * mm});
            skLineSegment(sketch, "E115.38", {"start": v(90, 96) * mm, "end": v(90, 100) * mm});
            skLineSegment(sketch, "E115.39", {"start": v(-30, 96) * mm, "end": v(-30, 100) * mm});
            skLineSegment(sketch, "E115.40", {"start": v(110, 100) * mm, "end": v(90, 100) * mm});
            skLineSegment(sketch, "E115.42", {"start": v(130, 96) * mm, "end": v(130, 100) * mm});
            skLineSegment(sketch, "E115.44", {"start": v(30, 96) * mm, "end": v(50, 96) * mm});
            skLineSegment(sketch, "E115.45", {"start": v(110, 96) * mm, "end": v(110, 100) * mm});
            skLineSegment(sketch, "E115.46", {"start": v(10, 96) * mm, "end": v(10, 100) * mm});
            skLineSegment(sketch, "E115.47", {"start": v(110, 96) * mm, "end": v(130, 96) * mm});
            skLineSegment(sketch, "E115.48", {"start": v(-10, 96) * mm, "end": v(-10, 100) * mm});
            skLineSegment(sketch, "E115.49", {"start": v(-130, 100) * mm, "end": v(-150, 100) * mm});
            skLineSegment(sketch, "E115.50", {"start": v(130, 100) * mm, "end": v(110, 100) * mm});
            skLineSegment(sketch, "E115.51", {"start": v(-110, 100) * mm, "end": v(-130, 100) * mm});
            skLineSegment(sketch, "E115.52", {"start": v(90, 100) * mm, "end": v(70, 100) * mm});
            skLineSegment(sketch, "E115.58", {"start": v(-10, 96) * mm, "end": v(10, 96) * mm});
            skLineSegment(sketch, "E115.59", {"start": v(-10, 96) * mm, "end": v(-10, 100) * mm});
            skLineSegment(sketch, "E115.60", {"start": v(10, 100) * mm, "end": v(-10, 100) * mm});
            skLineSegment(sketch, "E115.61", {"start": v(10, 96) * mm, "end": v(10, 100) * mm});
            skLineSegment(sketch, "E115.62", {"start": v(110, 96) * mm, "end": v(130, 96) * mm});
            skLineSegment(sketch, "E115.63", {"start": v(130, 96) * mm, "end": v(130, 100) * mm});
            skLineSegment(sketch, "E115.64", {"start": v(110, 96) * mm, "end": v(110, 100) * mm});
            skLineSegment(sketch, "E115.66", {"start": v(30, 96) * mm, "end": v(50, 96) * mm});
            skLineSegment(sketch, "E115.67", {"start": v(30, 96) * mm, "end": v(30, 100) * mm});
            skLineSegment(sketch, "E115.68", {"start": v(50, 100) * mm, "end": v(30, 100) * mm});
            skLineSegment(sketch, "E115.69", {"start": v(50, 96) * mm, "end": v(50, 100) * mm});
            skLineSegment(sketch, "E115.70", {"start": v(-130, 96) * mm, "end": v(-130, 100) * mm});
            skLineSegment(sketch, "E115.71", {"start": v(-130, 96) * mm, "end": v(-110, 96) * mm});
            skLineSegment(sketch, "E115.72", {"start": v(-110, 96) * mm, "end": v(-110, 100) * mm});
            skLineSegment(sketch, "E115.73", {"start": v(-30, 100) * mm, "end": v(-50, 100) * mm});
            skLineSegment(sketch, "E115.74", {"start": v(-50, 96) * mm, "end": v(-50, 100) * mm});
            skLineSegment(sketch, "E115.75", {"start": v(-30, 96) * mm, "end": v(-30, 100) * mm});
            skLineSegment(sketch, "E115.76", {"start": v(-50, 96) * mm, "end": v(-30, 96) * mm});
            skLineSegment(sketch, "E115.78", {"start": v(90, 96) * mm, "end": v(90, 100) * mm});
            skLineSegment(sketch, "E115.79", {"start": v(70, 96) * mm, "end": v(90, 96) * mm});
            skLineSegment(sketch, "E115.81", {"start": v(70, 96) * mm, "end": v(70, 100) * mm});
            skLineSegment(sketch, "E115.82", {"start": v(-90, 96) * mm, "end": v(-90, 100) * mm});
            skLineSegment(sketch, "E115.83", {"start": v(-90, 96) * mm, "end": v(-70, 96) * mm});
            skLineSegment(sketch, "E115.84", {"start": v(-70, 100) * mm, "end": v(-90, 100) * mm});
            skLineSegment(sketch, "E115.85", {"start": v(-70, 96) * mm, "end": v(-70, 100) * mm});
            skLineSegment(sketch, "E115.86", {"start": v(-90, 96) * mm, "end": v(-70, 96) * mm});
            skLineSegment(sketch, "E115.87", {"start": v(70, 96) * mm, "end": v(90, 96) * mm});
            skLineSegment(sketch, "E115.90", {"start": v(30, 96) * mm, "end": v(50, 96) * mm});
            skLineSegment(sketch, "E115.91", {"start": v(-110, 96) * mm, "end": v(-110, 100) * mm});
            skLineSegment(sketch, "E115.96", {"start": v(-70, 96) * mm, "end": v(-70, 100) * mm});
            skLineSegment(sketch, "E115.97", {"start": v(10, 96) * mm, "end": v(10, 100) * mm});
            skLineSegment(sketch, "E115.98", {"start": v(50, 96) * mm, "end": v(50, 100) * mm});
            skLineSegment(sketch, "E115.100", {"start": v(-50, 96) * mm, "end": v(-30, 96) * mm});
            skLineSegment(sketch, "E115.101", {"start": v(70, 96) * mm, "end": v(70, 100) * mm});
            skLineSegment(sketch, "E115.103", {"start": v(-30, 96) * mm, "end": v(-30, 100) * mm});
            skLineSegment(sketch, "E115.105", {"start": v(90, 96) * mm, "end": v(90, 100) * mm});
            skLineSegment(sketch, "E115.106", {"start": v(-10, 96) * mm, "end": v(10, 96) * mm});
            skLineSegment(sketch, "E115.112", {"start": v(-130, 96) * mm, "end": v(-110, 96) * mm});
            skLineSegment(sketch, "E115.115", {"start": v(110, 96) * mm, "end": v(130, 96) * mm});
            skLineSegment(sketch, "E115.118", {"start": v(30, 96) * mm, "end": v(30, 100) * mm});
            skLineSegment(sketch, "E115.119", {"start": v(130, 96) * mm, "end": v(130, 100) * mm});
            skLineSegment(sketch, "E115.127", {"start": v(-50, 96) * mm, "end": v(-50, 100) * mm});
            skLineSegment(sketch, "E115.128", {"start": v(-130, 96) * mm, "end": v(-130, 100) * mm});
            skLineSegment(sketch, "E115.129", {"start": v(110, 96) * mm, "end": v(110, 100) * mm});
            skLineSegment(sketch, "E115.130", {"start": v(-10, 96) * mm, "end": v(-10, 100) * mm});
            skLineSegment(sketch, "E115.131", {"start": v(-90, 96) * mm, "end": v(-90, 100) * mm});
            skLineSegment(sketch, "E115.132", {"start": v(10, 100) * mm, "end": v(10, 96) * mm});
            skLineSegment(sketch, "E115.134", {"start": v(10, 96) * mm, "end": v(-10, 96) * mm});
            skLineSegment(sketch, "E115.138", {"start": v(130, 96) * mm, "end": v(110, 96) * mm});
            skLineSegment(sketch, "E115.140", {"start": v(130, 100) * mm, "end": v(130, 96) * mm});
            skLineSegment(sketch, "E115.142", {"start": v(50, 96) * mm, "end": v(30, 96) * mm});
            skLineSegment(sketch, "E115.143", {"start": v(50, 100) * mm, "end": v(50, 96) * mm});
            skLineSegment(sketch, "E115.147", {"start": v(30, 100) * mm, "end": v(30, 96) * mm});
            skLineSegment(sketch, "E115.149", {"start": v(-110, 96) * mm, "end": v(-130, 96) * mm});
            skLineSegment(sketch, "E115.151", {"start": v(-110, 100) * mm, "end": v(-110, 96) * mm});
            skLineSegment(sketch, "E115.152", {"start": v(-30, 96) * mm, "end": v(-50, 96) * mm});
            skLineSegment(sketch, "E115.153", {"start": v(-30, 100) * mm, "end": v(-30, 96) * mm});
            skLineSegment(sketch, "E115.158", {"start": v(90, 100) * mm, "end": v(90, 96) * mm});
            skLineSegment(sketch, "E115.159", {"start": v(90, 96) * mm, "end": v(70, 96) * mm});
            skLineSegment(sketch, "E115.162", {"start": v(70, 100) * mm, "end": v(70, 96) * mm});
            skLineSegment(sketch, "E115.165", {"start": v(-70, 100) * mm, "end": v(-70, 96) * mm});
            skLineSegment(sketch, "E115.166", {"start": v(-70, 96) * mm, "end": v(-90, 96) * mm});
            skLineSegment(sketch, "E115.167", {"start": v(-10, 100) * mm, "end": v(-10, 96) * mm});
            skLineSegment(sketch, "E115.168", {"start": v(110, 100) * mm, "end": v(110, 96) * mm});
            skLineSegment(sketch, "E115.169", {"start": v(-130, 100) * mm, "end": v(-130, 96) * mm});
            skLineSegment(sketch, "E115.170", {"start": v(-50, 100) * mm, "end": v(-50, 96) * mm});
            skLineSegment(sketch, "E115.171", {"start": v(-90, 100) * mm, "end": v(-90, 96) * mm});
            skLineSegment(sketch, "E116.bottom", {"start": v(-150, 96) * mm, "end": v(150, 96) * mm});
            skLineSegment(sketch, "E116.top", {"start": v(-150, 100) * mm, "end": v(150, 100) * mm});
            skLineSegment(sketch, "E116.left", {"start": v(-150, 96) * mm, "end": v(-150, 100) * mm});
            skLineSegment(sketch, "E116.right", {"start": v(150, 96) * mm, "end": v(150, 100) * mm});
            skSolve(sketch);
        }
        {
            var Q0;
            Q0 = qSketchRegion(id + "F4", true);
            extrude(context, id + "F5", {"entities" : qUnion([Q0]), "depth" : 100 * mm});
        }
        {
            var Q0;
            Q0=makeQuery(id+"F5.opExtrude","SWEPT_BODY",BODY,{"disambiguationData":[OSD([sQuery(id+"F4.wireOp",EDGE,"E116.bottom"),sQuery(id+"F4.wireOp",EDGE,"E116.top"),sQuery(id+"F4.wireOp",EDGE,"E116.left"),sQuery(id+"F4.wireOp",EDGE,"E116.right")])]});
            var Q1;
            Q1=makeQuery(id+"F3.opExtrude","SWEPT_BODY",BODY,{"disambiguationData":[OSD([sQuery(id+"F2.wireOp",EDGE,"E113.46"),sQuery(id+"F2.wireOp",EDGE,"E113.49"),sQuery(id+"F2.wireOp",EDGE,"E113.76"),sQuery(id+"F2.wireOp",EDGE,"E114")])]});
            var Q2;
            Q2=makeQuery(id+"F3.opExtrude","SWEPT_BODY",BODY,{"disambiguationData":[OSD([sQuery(id+"F2.wireOp",EDGE,"E113.37"),sQuery(id+"F2.wireOp",EDGE,"E113.54"),sQuery(id+"F2.wireOp",EDGE,"E113.85"),sQuery(id+"F2.wireOp",EDGE,"E114")])]});
            var Q3;
            Q3=makeQuery(id+"F3.opExtrude","SWEPT_BODY",BODY,{"disambiguationData":[OSD([sQuery(id+"F2.wireOp",EDGE,"E113.42"),sQuery(id+"F2.wireOp",EDGE,"E113.62"),sQuery(id+"F2.wireOp",EDGE,"E113.67"),sQuery(id+"F2.wireOp",EDGE,"E114")])]});
            var Q4;
            Q4=makeQuery(id+"F3.opExtrude","SWEPT_BODY",BODY,{"disambiguationData":[OSD([sQuery(id+"F2.wireOp",EDGE,"E113.56"),sQuery(id+"F2.wireOp",EDGE,"E113.70"),sQuery(id+"F2.wireOp",EDGE,"E113.80"),sQuery(id+"F2.wireOp",EDGE,"E114")])]});
            var Q5;
            Q5=makeQuery(id+"F3.opExtrude","SWEPT_BODY",BODY,{"disambiguationData":[OSD([sQuery(id+"F2.wireOp",EDGE,"E113.47"),sQuery(id+"F2.wireOp",EDGE,"E113.57"),sQuery(id+"F2.wireOp",EDGE,"E113.83"),sQuery(id+"F2.wireOp",EDGE,"E114")])]});
            var Q6;
            Q6=makeQuery(id+"F3.opExtrude","SWEPT_BODY",BODY,{"disambiguationData":[OSD([sQuery(id+"F2.wireOp",EDGE,"E113.38"),sQuery(id+"F2.wireOp",EDGE,"E113.63"),sQuery(id+"F2.wireOp",EDGE,"E113.69"),sQuery(id+"F2.wireOp",EDGE,"E114")])]});
            var Q7;
            Q7=makeQuery(id+"F3.opExtrude","SWEPT_BODY",BODY,{"disambiguationData":[OSD([sQuery(id+"F2.wireOp",EDGE,"E113.55"),sQuery(id+"F2.wireOp",EDGE,"E113.79"),sQuery(id+"F2.wireOp",EDGE,"E113.84"),sQuery(id+"F2.wireOp",EDGE,"E114")])]});
            booleanBodies(context, id + "F6", {"operationType" : BooleanOperationType.UNION, "tools" : qUnion([Q0, Q1, Q2, Q3, Q4, Q5, Q6, Q7])});
        }
        {
            var Q0;
            Q0=makeQuery(id+"F1.opExtrude","CAP_FACE",FACE,{"disambiguationData":[OSD([sQuery(id+"F0.wireOp",EDGE,"E0.bottom"),sQuery(id+"F0.wireOp",EDGE,"E0.top"),sQuery(id+"F0.wireOp",EDGE,"E0.left"),sQuery(id+"F0.wireOp",EDGE,"E0.right"),sQuery(id+"F0.wireOp",EDGE,"E6.1.0.0"),sQuery(id+"F0.wireOp",EDGE,"E6.1.0.1"),sQuery(id+"F0.wireOp",EDGE,"E6.1.0.2"),sQuery(id+"F0.wireOp",EDGE,"E6.1.0.3"),sQuery(id+"F0.wireOp",EDGE,"E6.2.0.0"),sQuery(id+"F0.wireOp",EDGE,"E6.2.0.1"),sQuery(id+"F0.wireOp",EDGE,"E6.2.0.2"),sQuery(id+"F0.wireOp",EDGE,"E6.2.0.3"),sQuery(id+"F0.wireOp",EDGE,"E6.3.0.0"),sQuery(id+"F0.wireOp",EDGE,"E6.3.0.1"),sQuery(id+"F0.wireOp",EDGE,"E6.3.0.2"),sQuery(id+"F0.wireOp",EDGE,"E6.3.0.3"),sQuery(id+"F0.wireOp",EDGE,"E7.MirrorCS"),sQuery(id+"F0.wireOp",EDGE,"E8.MirrorCS"),sQuery(id+"F0.wireOp",EDGE,"E9.MirrorCS"),sQuery(id+"F0.wireOp",EDGE,"E10.MirrorCS"),sQuery(id+"F0.wireOp",EDGE,"E2"),sQuery(id+"F0.wireOp",EDGE,"E3"),sQuery(id+"F0.wireOp",EDGE,"E4.MirrorCS"),sQuery(id+"F0.wireOp",EDGE,"E5.MirrorCS"),sQuery(id+"F0.wireOp",EDGE,"E11.MirrorCS"),sQuery(id+"F0.wireOp",EDGE,"E12.MirrorCS"),sQuery(id+"F0.wireOp",EDGE,"E13.MirrorCS"),sQuery(id+"F0.wireOp",EDGE,"E15.MirrorCS"),sQuery(id+"F0.wireOp",EDGE,"E16.MirrorCS"),sQuery(id+"F0.wireOp",EDGE,"E17.MirrorCS"),sQuery(id+"F0.wireOp",EDGE,"E18.MirrorCS"),sQuery(id+"F0.wireOp",EDGE,"E19.MirrorCS"),sQuery(id+"F0.wireOp",EDGE,"E22.MirrorCS"),sQuery(id+"F0.wireOp",EDGE,"E21.MirrorCS"),sQuery(id+"F0.wireOp",EDGE,"E25.MirrorCS"),sQuery(id+"F0.wireOp",EDGE,"E23.MirrorCS"),sQuery(id+"F0.wireOp",EDGE,"E26.MirrorCS"),sQuery(id+"F0.wireOp",EDGE,"E27.MirrorCS"),sQuery(id+"F0.wireOp",EDGE,"E28.MirrorCS"),sQuery(id+"F0.wireOp",EDGE,"E24.MirrorCS"),sQuery(id+"F0.wireOp",EDGE,"E29.MirrorCS"),sQuery(id+"F0.wireOp",EDGE,"E30.MirrorCS"),sQuery(id+"F0.wireOp",EDGE,"E31.MirrorCS"),sQuery(id+"F0.wireOp",EDGE,"E32.MirrorCS"),sQuery(id+"F0.wireOp",EDGE,"E33.MirrorCS"),sQuery(id+"F0.wireOp",EDGE,"E34.MirrorCS"),sQuery(id+"F0.wireOp",EDGE,"E35.MirrorCS"),sQuery(id+"F0.wireOp",EDGE,"E36.MirrorCS"),sQuery(id+"F0.wireOp",EDGE,"E37.MirrorCS"),sQuery(id+"F0.wireOp",EDGE,"E38.MirrorCS"),sQuery(id+"F0.wireOp",EDGE,"E39.MirrorCS"),sQuery(id+"F0.wireOp",EDGE,"E40.MirrorCS"),sQuery(id+"F0.wireOp",EDGE,"E41.MirrorCS"),sQuery(id+"F0.wireOp",EDGE,"E42.MirrorCS"),sQuery(id+"F0.wireOp",EDGE,"E44.MirrorCS"),sQuery(id+"F0.wireOp",EDGE,"E45.MirrorCS"),sQuery(id+"F0.wireOp",EDGE,"E46.MirrorCS"),sQuery(id+"F0.wireOp",EDGE,"E47.MirrorCS"),sQuery(id+"F0.wireOp",EDGE,"E48.MirrorCS"),sQuery(id+"F0.wireOp",EDGE,"E49.MirrorCS"),sQuery(id+"F0.wireOp",EDGE,"E56.0.1.0"),sQuery(id+"F0.wireOp",EDGE,"E56.0.1.1"),sQuery(id+"F0.wireOp",EDGE,"E56.0.1.2"),sQuery(id+"F0.wireOp",EDGE,"E56.0.1.3"),sQuery(id+"F0.wireOp",EDGE,"E56.0.2.0"),sQuery(id+"F0.wireOp",EDGE,"E56.0.2.1"),sQuery(id+"F0.wireOp",EDGE,"E56.0.2.2"),sQuery(id+"F0.wireOp",EDGE,"E56.0.2.3"),sQuery(id+"F0.wireOp",EDGE,"E53"),sQuery(id+"F0.wireOp",EDGE,"E57.MirrorCS"),sQuery(id+"F0.wireOp",EDGE,"E55.MirrorCS"),sQuery(id+"F0.wireOp",EDGE,"E58.MirrorCS"),sQuery(id+"F0.wireOp",EDGE,"E59.MirrorCS"),sQuery(id+"F0.wireOp",EDGE,"E60.MirrorCS"),sQuery(id+"F0.wireOp",EDGE,"E61.MirrorCS"),sQuery(id+"F0.wireOp",EDGE,"E62.MirrorCS"),sQuery(id+"F0.wireOp",EDGE,"E52"),sQuery(id+"F0.wireOp",EDGE,"E63.MirrorCS"),sQuery(id+"F0.wireOp",EDGE,"E64.MirrorCS"),sQuery(id+"F0.wireOp",EDGE,"E54.MirrorCS"),sQuery(id+"F0.wireOp",EDGE,"E66.MirrorCS"),sQuery(id+"F0.wireOp",EDGE,"E67.MirrorCS"),sQuery(id+"F0.wireOp",EDGE,"E69.MirrorCS"),sQuery(id+"F0.wireOp",EDGE,"E70.MirrorCS"),sQuery(id+"F0.wireOp",EDGE,"E71.MirrorCS"),sQuery(id+"F0.wireOp",EDGE,"E72.MirrorCS"),sQuery(id+"F0.wireOp",EDGE,"E74.MirrorCS"),sQuery(id+"F0.wireOp",EDGE,"E75.MirrorCS"),sQuery(id+"F0.wireOp",EDGE,"E76.MirrorCS"),sQuery(id+"F0.wireOp",EDGE,"E78.MirrorCS"),sQuery(id+"F0.wireOp",EDGE,"E73.MirrorCS"),sQuery(id+"F0.wireOp",EDGE,"E79.MirrorCS"),sQuery(id+"F0.wireOp",EDGE,"E80.MirrorCS"),sQuery(id+"F0.wireOp",EDGE,"E77.MirrorCS"),sQuery(id+"F0.wireOp",EDGE,"E81.MirrorCS"),sQuery(id+"F0.wireOp",EDGE,"E82.MirrorCS"),sQuery(id+"F0.wireOp",EDGE,"E83.MirrorCS"),sQuery(id+"F0.wireOp",EDGE,"E85.MirrorCS"),sQuery(id+"F0.wireOp",EDGE,"E86.MirrorCS"),sQuery(id+"F0.wireOp",EDGE,"E87.MirrorCS"),sQuery(id+"F0.wireOp",EDGE,"E88.trimOffspring"),sQuery(id+"F0.wireOp",EDGE,"E89.trimOffspring"),sQuery(id+"F0.wireOp",EDGE,"E90.trimOffspring"),sQuery(id+"F0.wireOp",EDGE,"E91.trimOffspring"),sQuery(id+"F0.wireOp",EDGE,"E92.trimOffspring"),sQuery(id+"F0.wireOp",EDGE,"E93.trimOffspring"),sQuery(id+"F0.wireOp",EDGE,"E94.trimOffspring"),sQuery(id+"F0.wireOp",EDGE,"E95.trimOffspring"),sQuery(id+"F0.wireOp",EDGE,"E96.trimOffspring"),sQuery(id+"F0.wireOp",EDGE,"E97.trimOffspring"),sQuery(id+"F0.wireOp",EDGE,"E98.trimOffspring"),sQuery(id+"F0.wireOp",EDGE,"E99.trimOffspring"),sQuery(id+"F0.wireOp",EDGE,"E100.trimOffspring"),sQuery(id+"F0.wireOp",EDGE,"E101.trimOffspring"),sQuery(id+"F0.wireOp",EDGE,"E102.trimOffspring"),sQuery(id+"F0.wireOp",EDGE,"E103.trimOffspring"),sQuery(id+"F0.wireOp",EDGE,"E104.trimOffspring"),sQuery(id+"F0.wireOp",EDGE,"E105.trimOffspring"),sQuery(id+"F0.wireOp",EDGE,"E106.trimOffspring"),sQuery(id+"F0.wireOp",EDGE,"E107.trimOffspring"),sQuery(id+"F0.wireOp",EDGE,"E109.trimOffspring"),sQuery(id+"F0.wireOp",EDGE,"E110.trimOffspring"),sQuery(id+"F0.wireOp",EDGE,"E111.trimOffspring"),sQuery(id+"F0.wireOp",EDGE,"E112.trimOffspring")])],"isStart":false});
            var sketch = newSketch(context, id + "F7", { "sketchPlane" : qUnion([Q0])});
            skLineSegment(sketch, "E117.0", {"start": v(-146, -90) * mm, "end": v(-150, -90) * mm});
            skLineSegment(sketch, "E117.2", {"start": v(-150, -90) * mm, "end": v(-150, -100) * mm});
            skLineSegment(sketch, "E117.3", {"start": v(-150, 30) * mm, "end": v(-150, 10) * mm});
            skLineSegment(sketch, "E117.4", {"start": v(-146, -50) * mm, "end": v(-146, -30) * mm});
            skLineSegment(sketch, "E117.5", {"start": v(-146, -70) * mm, "end": v(-150, -70) * mm});
            skLineSegment(sketch, "E117.6", {"start": v(-146, 70) * mm, "end": v(-150, 70) * mm});
            skLineSegment(sketch, "E117.7", {"start": v(-146, -50) * mm, "end": v(-150, -50) * mm});
            skLineSegment(sketch, "E117.8", {"start": v(-146, -10) * mm, "end": v(-150, -10) * mm});
            skLineSegment(sketch, "E117.9", {"start": v(-146, 30) * mm, "end": v(-150, 30) * mm});
            skLineSegment(sketch, "E117.10", {"start": v(-146, 30) * mm, "end": v(-146, 50) * mm});
            skLineSegment(sketch, "E117.11", {"start": v(-146, 50) * mm, "end": v(-150, 50) * mm});
            skLineSegment(sketch, "E117.13", {"start": v(-146, 10) * mm, "end": v(-150, 10) * mm});
            skLineSegment(sketch, "E117.14", {"start": v(-146, -30) * mm, "end": v(-150, -30) * mm});
            skLineSegment(sketch, "E117.15", {"start": v(-150, -50) * mm, "end": v(-150, -70) * mm});
            skLineSegment(sketch, "E117.16", {"start": v(-146, -90) * mm, "end": v(-146, -70) * mm});
            skLineSegment(sketch, "E117.17", {"start": v(-146, 70) * mm, "end": v(-146, 90) * mm});
            skLineSegment(sketch, "E117.18", {"start": v(-150, 100) * mm, "end": v(-150, 90) * mm});
            skLineSegment(sketch, "E117.19", {"start": v(-146, 90) * mm, "end": v(-150, 90) * mm});
            skLineSegment(sketch, "E117.20", {"start": v(-146, 10) * mm, "end": v(-146, -10) * mm});
            skLineSegment(sketch, "E117.21", {"start": v(-150, 70) * mm, "end": v(-150, 50) * mm});
            skLineSegment(sketch, "E117.22", {"start": v(-150, -10) * mm, "end": v(-150, -30) * mm});
            skLineSegment(sketch, "E117.23", {"start": v(-146, -70) * mm, "end": v(-150, -70) * mm});
            skLineSegment(sketch, "E117.24", {"start": v(-146, 50) * mm, "end": v(-150, 50) * mm});
            skLineSegment(sketch, "E117.25", {"start": v(-146, -90) * mm, "end": v(-150, -90) * mm});
            skLineSegment(sketch, "E117.26", {"start": v(-146, 70) * mm, "end": v(-150, 70) * mm});
            skLineSegment(sketch, "E117.27", {"start": v(-146, -50) * mm, "end": v(-150, -50) * mm});
            skLineSegment(sketch, "E117.28", {"start": v(-150, -50) * mm, "end": v(-150, -70) * mm});
            skLineSegment(sketch, "E117.29", {"start": v(-146, -30) * mm, "end": v(-150, -30) * mm});
            skLineSegment(sketch, "E117.35", {"start": v(-146, 70) * mm, "end": v(-146, 90) * mm});
            skLineSegment(sketch, "E117.36", {"start": v(-146, -90) * mm, "end": v(-146, -70) * mm});
            skLineSegment(sketch, "E117.37", {"start": v(-150, -90) * mm, "end": v(-150, -100) * mm});
            skLineSegment(sketch, "E117.38", {"start": v(-146, 30) * mm, "end": v(-150, 30) * mm});
            skLineSegment(sketch, "E117.40", {"start": v(-146, 30) * mm, "end": v(-146, 50) * mm});
            skLineSegment(sketch, "E117.49", {"start": v(-146, -10) * mm, "end": v(-150, -10) * mm});
            skLineSegment(sketch, "E117.53", {"start": v(-150, 100) * mm, "end": v(-150, 90) * mm});
            skLineSegment(sketch, "E117.54", {"start": v(-146, 90) * mm, "end": v(-150, 90) * mm});
            skLineSegment(sketch, "E117.55", {"start": v(-146, 10) * mm, "end": v(-146, -10) * mm});
            skLineSegment(sketch, "E117.56", {"start": v(-150, 70) * mm, "end": v(-150, 50) * mm});
            skLineSegment(sketch, "E117.57", {"start": v(-150, -10) * mm, "end": v(-150, -30) * mm});
            skLineSegment(sketch, "E117.60", {"start": v(-146, 10) * mm, "end": v(-150, 10) * mm});
            skLineSegment(sketch, "E117.61", {"start": v(-146, -50) * mm, "end": v(-146, -30) * mm});
            skLineSegment(sketch, "E117.62", {"start": v(-150, 30) * mm, "end": v(-150, 10) * mm});
            skLineSegment(sketch, "E118", {"start": v(-150, 100) * mm, "end": v(-150, -100) * mm});
            skSolve(sketch);
        }
        {
            var Q0;
            Q0 = qSketchRegion(id + "F7", true);
            var Q1;
            Q1=makeQuery(id+"F1.opExtrude","CAP_FACE",FACE,{"disambiguationData":[OSD([sQuery(id+"F0.wireOp",EDGE,"E0.bottom"),sQuery(id+"F0.wireOp",EDGE,"E0.top"),sQuery(id+"F0.wireOp",EDGE,"E0.left"),sQuery(id+"F0.wireOp",EDGE,"E0.right"),sQuery(id+"F0.wireOp",EDGE,"E6.1.0.0"),sQuery(id+"F0.wireOp",EDGE,"E6.1.0.1"),sQuery(id+"F0.wireOp",EDGE,"E6.1.0.2"),sQuery(id+"F0.wireOp",EDGE,"E6.1.0.3"),sQuery(id+"F0.wireOp",EDGE,"E6.2.0.0"),sQuery(id+"F0.wireOp",EDGE,"E6.2.0.1"),sQuery(id+"F0.wireOp",EDGE,"E6.2.0.2"),sQuery(id+"F0.wireOp",EDGE,"E6.2.0.3"),sQuery(id+"F0.wireOp",EDGE,"E6.3.0.0"),sQuery(id+"F0.wireOp",EDGE,"E6.3.0.1"),sQuery(id+"F0.wireOp",EDGE,"E6.3.0.2"),sQuery(id+"F0.wireOp",EDGE,"E6.3.0.3"),sQuery(id+"F0.wireOp",EDGE,"E7.MirrorCS"),sQuery(id+"F0.wireOp",EDGE,"E8.MirrorCS"),sQuery(id+"F0.wireOp",EDGE,"E9.MirrorCS"),sQuery(id+"F0.wireOp",EDGE,"E10.MirrorCS"),sQuery(id+"F0.wireOp",EDGE,"E2"),sQuery(id+"F0.wireOp",EDGE,"E3"),sQuery(id+"F0.wireOp",EDGE,"E4.MirrorCS"),sQuery(id+"F0.wireOp",EDGE,"E5.MirrorCS"),sQuery(id+"F0.wireOp",EDGE,"E11.MirrorCS"),sQuery(id+"F0.wireOp",EDGE,"E12.MirrorCS"),sQuery(id+"F0.wireOp",EDGE,"E13.MirrorCS"),sQuery(id+"F0.wireOp",EDGE,"E15.MirrorCS"),sQuery(id+"F0.wireOp",EDGE,"E16.MirrorCS"),sQuery(id+"F0.wireOp",EDGE,"E17.MirrorCS"),sQuery(id+"F0.wireOp",EDGE,"E18.MirrorCS"),sQuery(id+"F0.wireOp",EDGE,"E19.MirrorCS"),sQuery(id+"F0.wireOp",EDGE,"E22.MirrorCS"),sQuery(id+"F0.wireOp",EDGE,"E21.MirrorCS"),sQuery(id+"F0.wireOp",EDGE,"E25.MirrorCS"),sQuery(id+"F0.wireOp",EDGE,"E23.MirrorCS"),sQuery(id+"F0.wireOp",EDGE,"E26.MirrorCS"),sQuery(id+"F0.wireOp",EDGE,"E27.MirrorCS"),sQuery(id+"F0.wireOp",EDGE,"E28.MirrorCS"),sQuery(id+"F0.wireOp",EDGE,"E24.MirrorCS"),sQuery(id+"F0.wireOp",EDGE,"E29.MirrorCS"),sQuery(id+"F0.wireOp",EDGE,"E30.MirrorCS"),sQuery(id+"F0.wireOp",EDGE,"E31.MirrorCS"),sQuery(id+"F0.wireOp",EDGE,"E32.MirrorCS"),sQuery(id+"F0.wireOp",EDGE,"E33.MirrorCS"),sQuery(id+"F0.wireOp",EDGE,"E34.MirrorCS"),sQuery(id+"F0.wireOp",EDGE,"E35.MirrorCS"),sQuery(id+"F0.wireOp",EDGE,"E36.MirrorCS"),sQuery(id+"F0.wireOp",EDGE,"E37.MirrorCS"),sQuery(id+"F0.wireOp",EDGE,"E38.MirrorCS"),sQuery(id+"F0.wireOp",EDGE,"E39.MirrorCS"),sQuery(id+"F0.wireOp",EDGE,"E40.MirrorCS"),sQuery(id+"F0.wireOp",EDGE,"E41.MirrorCS"),sQuery(id+"F0.wireOp",EDGE,"E42.MirrorCS"),sQuery(id+"F0.wireOp",EDGE,"E44.MirrorCS"),sQuery(id+"F0.wireOp",EDGE,"E45.MirrorCS"),sQuery(id+"F0.wireOp",EDGE,"E46.MirrorCS"),sQuery(id+"F0.wireOp",EDGE,"E47.MirrorCS"),sQuery(id+"F0.wireOp",EDGE,"E48.MirrorCS"),sQuery(id+"F0.wireOp",EDGE,"E49.MirrorCS"),sQuery(id+"F0.wireOp",EDGE,"E56.0.1.0"),sQuery(id+"F0.wireOp",EDGE,"E56.0.1.1"),sQuery(id+"F0.wireOp",EDGE,"E56.0.1.2"),sQuery(id+"F0.wireOp",EDGE,"E56.0.1.3"),sQuery(id+"F0.wireOp",EDGE,"E56.0.2.0"),sQuery(id+"F0.wireOp",EDGE,"E56.0.2.1"),sQuery(id+"F0.wireOp",EDGE,"E56.0.2.2"),sQuery(id+"F0.wireOp",EDGE,"E56.0.2.3"),sQuery(id+"F0.wireOp",EDGE,"E53"),sQuery(id+"F0.wireOp",EDGE,"E57.MirrorCS"),sQuery(id+"F0.wireOp",EDGE,"E55.MirrorCS"),sQuery(id+"F0.wireOp",EDGE,"E58.MirrorCS"),sQuery(id+"F0.wireOp",EDGE,"E59.MirrorCS"),sQuery(id+"F0.wireOp",EDGE,"E60.MirrorCS"),sQuery(id+"F0.wireOp",EDGE,"E61.MirrorCS"),sQuery(id+"F0.wireOp",EDGE,"E62.MirrorCS"),sQuery(id+"F0.wireOp",EDGE,"E52"),sQuery(id+"F0.wireOp",EDGE,"E63.MirrorCS"),sQuery(id+"F0.wireOp",EDGE,"E64.MirrorCS"),sQuery(id+"F0.wireOp",EDGE,"E54.MirrorCS"),sQuery(id+"F0.wireOp",EDGE,"E66.MirrorCS"),sQuery(id+"F0.wireOp",EDGE,"E67.MirrorCS"),sQuery(id+"F0.wireOp",EDGE,"E69.MirrorCS"),sQuery(id+"F0.wireOp",EDGE,"E70.MirrorCS"),sQuery(id+"F0.wireOp",EDGE,"E71.MirrorCS"),sQuery(id+"F0.wireOp",EDGE,"E72.MirrorCS"),sQuery(id+"F0.wireOp",EDGE,"E74.MirrorCS"),sQuery(id+"F0.wireOp",EDGE,"E75.MirrorCS"),sQuery(id+"F0.wireOp",EDGE,"E76.MirrorCS"),sQuery(id+"F0.wireOp",EDGE,"E78.MirrorCS"),sQuery(id+"F0.wireOp",EDGE,"E73.MirrorCS"),sQuery(id+"F0.wireOp",EDGE,"E79.MirrorCS"),sQuery(id+"F0.wireOp",EDGE,"E80.MirrorCS"),sQuery(id+"F0.wireOp",EDGE,"E77.MirrorCS"),sQuery(id+"F0.wireOp",EDGE,"E81.MirrorCS"),sQuery(id+"F0.wireOp",EDGE,"E82.MirrorCS"),sQuery(id+"F0.wireOp",EDGE,"E83.MirrorCS"),sQuery(id+"F0.wireOp",EDGE,"E85.MirrorCS"),sQuery(id+"F0.wireOp",EDGE,"E86.MirrorCS"),sQuery(id+"F0.wireOp",EDGE,"E87.MirrorCS"),sQuery(id+"F0.wireOp",EDGE,"E88.trimOffspring"),sQuery(id+"F0.wireOp",EDGE,"E89.trimOffspring"),sQuery(id+"F0.wireOp",EDGE,"E90.trimOffspring"),sQuery(id+"F0.wireOp",EDGE,"E91.trimOffspring"),sQuery(id+"F0.wireOp",EDGE,"E92.trimOffspring"),sQuery(id+"F0.wireOp",EDGE,"E93.trimOffspring"),sQuery(id+"F0.wireOp",EDGE,"E94.trimOffspring"),sQuery(id+"F0.wireOp",EDGE,"E95.trimOffspring"),sQuery(id+"F0.wireOp",EDGE,"E96.trimOffspring"),sQuery(id+"F0.wireOp",EDGE,"E97.trimOffspring"),sQuery(id+"F0.wireOp",EDGE,"E98.trimOffspring"),sQuery(id+"F0.wireOp",EDGE,"E99.trimOffspring"),sQuery(id+"F0.wireOp",EDGE,"E100.trimOffspring"),sQuery(id+"F0.wireOp",EDGE,"E101.trimOffspring"),sQuery(id+"F0.wireOp",EDGE,"E102.trimOffspring"),sQuery(id+"F0.wireOp",EDGE,"E103.trimOffspring"),sQuery(id+"F0.wireOp",EDGE,"E104.trimOffspring"),sQuery(id+"F0.wireOp",EDGE,"E105.trimOffspring"),sQuery(id+"F0.wireOp",EDGE,"E106.trimOffspring"),sQuery(id+"F0.wireOp",EDGE,"E107.trimOffspring"),sQuery(id+"F0.wireOp",EDGE,"E109.trimOffspring"),sQuery(id+"F0.wireOp",EDGE,"E110.trimOffspring"),sQuery(id+"F0.wireOp",EDGE,"E111.trimOffspring"),sQuery(id+"F0.wireOp",EDGE,"E112.trimOffspring")])],"isStart":true});
            extrude(context, id + "F8", {"entities" : qUnion([Q0]), "endBound" : BoundingType.UP_TO_SURFACE, "oppositeDirection" : true, "endBoundEntityFace" : qUnion([Q1]), "depth" : 25 * mm});
        }
        {
            var Q0;
            Q0=makeQuery(id+"F1.opExtrude","CAP_FACE",FACE,{"disambiguationData":[OSD([sQuery(id+"F0.wireOp",EDGE,"E0.bottom"),sQuery(id+"F0.wireOp",EDGE,"E0.top"),sQuery(id+"F0.wireOp",EDGE,"E0.left"),sQuery(id+"F0.wireOp",EDGE,"E0.right"),sQuery(id+"F0.wireOp",EDGE,"E6.1.0.0"),sQuery(id+"F0.wireOp",EDGE,"E6.1.0.1"),sQuery(id+"F0.wireOp",EDGE,"E6.1.0.2"),sQuery(id+"F0.wireOp",EDGE,"E6.1.0.3"),sQuery(id+"F0.wireOp",EDGE,"E6.2.0.0"),sQuery(id+"F0.wireOp",EDGE,"E6.2.0.1"),sQuery(id+"F0.wireOp",EDGE,"E6.2.0.2"),sQuery(id+"F0.wireOp",EDGE,"E6.2.0.3"),sQuery(id+"F0.wireOp",EDGE,"E6.3.0.0"),sQuery(id+"F0.wireOp",EDGE,"E6.3.0.1"),sQuery(id+"F0.wireOp",EDGE,"E6.3.0.2"),sQuery(id+"F0.wireOp",EDGE,"E6.3.0.3"),sQuery(id+"F0.wireOp",EDGE,"E7.MirrorCS"),sQuery(id+"F0.wireOp",EDGE,"E8.MirrorCS"),sQuery(id+"F0.wireOp",EDGE,"E9.MirrorCS"),sQuery(id+"F0.wireOp",EDGE,"E10.MirrorCS"),sQuery(id+"F0.wireOp",EDGE,"E2"),sQuery(id+"F0.wireOp",EDGE,"E3"),sQuery(id+"F0.wireOp",EDGE,"E4.MirrorCS"),sQuery(id+"F0.wireOp",EDGE,"E5.MirrorCS"),sQuery(id+"F0.wireOp",EDGE,"E11.MirrorCS"),sQuery(id+"F0.wireOp",EDGE,"E12.MirrorCS"),sQuery(id+"F0.wireOp",EDGE,"E13.MirrorCS"),sQuery(id+"F0.wireOp",EDGE,"E15.MirrorCS"),sQuery(id+"F0.wireOp",EDGE,"E16.MirrorCS"),sQuery(id+"F0.wireOp",EDGE,"E17.MirrorCS"),sQuery(id+"F0.wireOp",EDGE,"E18.MirrorCS"),sQuery(id+"F0.wireOp",EDGE,"E19.MirrorCS"),sQuery(id+"F0.wireOp",EDGE,"E22.MirrorCS"),sQuery(id+"F0.wireOp",EDGE,"E21.MirrorCS"),sQuery(id+"F0.wireOp",EDGE,"E25.MirrorCS"),sQuery(id+"F0.wireOp",EDGE,"E23.MirrorCS"),sQuery(id+"F0.wireOp",EDGE,"E26.MirrorCS"),sQuery(id+"F0.wireOp",EDGE,"E27.MirrorCS"),sQuery(id+"F0.wireOp",EDGE,"E28.MirrorCS"),sQuery(id+"F0.wireOp",EDGE,"E24.MirrorCS"),sQuery(id+"F0.wireOp",EDGE,"E29.MirrorCS"),sQuery(id+"F0.wireOp",EDGE,"E30.MirrorCS"),sQuery(id+"F0.wireOp",EDGE,"E31.MirrorCS"),sQuery(id+"F0.wireOp",EDGE,"E32.MirrorCS"),sQuery(id+"F0.wireOp",EDGE,"E33.MirrorCS"),sQuery(id+"F0.wireOp",EDGE,"E34.MirrorCS"),sQuery(id+"F0.wireOp",EDGE,"E35.MirrorCS"),sQuery(id+"F0.wireOp",EDGE,"E36.MirrorCS"),sQuery(id+"F0.wireOp",EDGE,"E37.MirrorCS"),sQuery(id+"F0.wireOp",EDGE,"E38.MirrorCS"),sQuery(id+"F0.wireOp",EDGE,"E39.MirrorCS"),sQuery(id+"F0.wireOp",EDGE,"E40.MirrorCS"),sQuery(id+"F0.wireOp",EDGE,"E41.MirrorCS"),sQuery(id+"F0.wireOp",EDGE,"E42.MirrorCS"),sQuery(id+"F0.wireOp",EDGE,"E44.MirrorCS"),sQuery(id+"F0.wireOp",EDGE,"E45.MirrorCS"),sQuery(id+"F0.wireOp",EDGE,"E46.MirrorCS"),sQuery(id+"F0.wireOp",EDGE,"E47.MirrorCS"),sQuery(id+"F0.wireOp",EDGE,"E48.MirrorCS"),sQuery(id+"F0.wireOp",EDGE,"E49.MirrorCS"),sQuery(id+"F0.wireOp",EDGE,"E56.0.1.0"),sQuery(id+"F0.wireOp",EDGE,"E56.0.1.1"),sQuery(id+"F0.wireOp",EDGE,"E56.0.1.2"),sQuery(id+"F0.wireOp",EDGE,"E56.0.1.3"),sQuery(id+"F0.wireOp",EDGE,"E56.0.2.0"),sQuery(id+"F0.wireOp",EDGE,"E56.0.2.1"),sQuery(id+"F0.wireOp",EDGE,"E56.0.2.2"),sQuery(id+"F0.wireOp",EDGE,"E56.0.2.3"),sQuery(id+"F0.wireOp",EDGE,"E53"),sQuery(id+"F0.wireOp",EDGE,"E57.MirrorCS"),sQuery(id+"F0.wireOp",EDGE,"E55.MirrorCS"),sQuery(id+"F0.wireOp",EDGE,"E58.MirrorCS"),sQuery(id+"F0.wireOp",EDGE,"E59.MirrorCS"),sQuery(id+"F0.wireOp",EDGE,"E60.MirrorCS"),sQuery(id+"F0.wireOp",EDGE,"E61.MirrorCS"),sQuery(id+"F0.wireOp",EDGE,"E62.MirrorCS"),sQuery(id+"F0.wireOp",EDGE,"E52"),sQuery(id+"F0.wireOp",EDGE,"E63.MirrorCS"),sQuery(id+"F0.wireOp",EDGE,"E64.MirrorCS"),sQuery(id+"F0.wireOp",EDGE,"E54.MirrorCS"),sQuery(id+"F0.wireOp",EDGE,"E66.MirrorCS"),sQuery(id+"F0.wireOp",EDGE,"E67.MirrorCS"),sQuery(id+"F0.wireOp",EDGE,"E69.MirrorCS"),sQuery(id+"F0.wireOp",EDGE,"E70.MirrorCS"),sQuery(id+"F0.wireOp",EDGE,"E71.MirrorCS"),sQuery(id+"F0.wireOp",EDGE,"E72.MirrorCS"),sQuery(id+"F0.wireOp",EDGE,"E74.MirrorCS"),sQuery(id+"F0.wireOp",EDGE,"E75.MirrorCS"),sQuery(id+"F0.wireOp",EDGE,"E76.MirrorCS"),sQuery(id+"F0.wireOp",EDGE,"E78.MirrorCS"),sQuery(id+"F0.wireOp",EDGE,"E73.MirrorCS"),sQuery(id+"F0.wireOp",EDGE,"E79.MirrorCS"),sQuery(id+"F0.wireOp",EDGE,"E80.MirrorCS"),sQuery(id+"F0.wireOp",EDGE,"E77.MirrorCS"),sQuery(id+"F0.wireOp",EDGE,"E81.MirrorCS"),sQuery(id+"F0.wireOp",EDGE,"E82.MirrorCS"),sQuery(id+"F0.wireOp",EDGE,"E83.MirrorCS"),sQuery(id+"F0.wireOp",EDGE,"E85.MirrorCS"),sQuery(id+"F0.wireOp",EDGE,"E86.MirrorCS"),sQuery(id+"F0.wireOp",EDGE,"E87.MirrorCS"),sQuery(id+"F0.wireOp",EDGE,"E88.trimOffspring"),sQuery(id+"F0.wireOp",EDGE,"E89.trimOffspring"),sQuery(id+"F0.wireOp",EDGE,"E90.trimOffspring"),sQuery(id+"F0.wireOp",EDGE,"E91.trimOffspring"),sQuery(id+"F0.wireOp",EDGE,"E92.trimOffspring"),sQuery(id+"F0.wireOp",EDGE,"E93.trimOffspring"),sQuery(id+"F0.wireOp",EDGE,"E94.trimOffspring"),sQuery(id+"F0.wireOp",EDGE,"E95.trimOffspring"),sQuery(id+"F0.wireOp",EDGE,"E96.trimOffspring"),sQuery(id+"F0.wireOp",EDGE,"E97.trimOffspring"),sQuery(id+"F0.wireOp",EDGE,"E98.trimOffspring"),sQuery(id+"F0.wireOp",EDGE,"E99.trimOffspring"),sQuery(id+"F0.wireOp",EDGE,"E100.trimOffspring"),sQuery(id+"F0.wireOp",EDGE,"E101.trimOffspring"),sQuery(id+"F0.wireOp",EDGE,"E102.trimOffspring"),sQuery(id+"F0.wireOp",EDGE,"E103.trimOffspring"),sQuery(id+"F0.wireOp",EDGE,"E104.trimOffspring"),sQuery(id+"F0.wireOp",EDGE,"E105.trimOffspring"),sQuery(id+"F0.wireOp",EDGE,"E106.trimOffspring"),sQuery(id+"F0.wireOp",EDGE,"E107.trimOffspring"),sQuery(id+"F0.wireOp",EDGE,"E109.trimOffspring"),sQuery(id+"F0.wireOp",EDGE,"E110.trimOffspring"),sQuery(id+"F0.wireOp",EDGE,"E111.trimOffspring"),sQuery(id+"F0.wireOp",EDGE,"E112.trimOffspring")])],"isStart":false});
            var sketch = newSketch(context, id + "F9", { "sketchPlane" : qUnion([Q0])});
            skLineSegment(sketch, "E119.0", {"start": v(-146, -90) * mm, "end": v(-150, -90) * mm});
            skLineSegment(sketch, "E119.1", {"start": v(-150, -90) * mm, "end": v(-150, -100) * mm});
            skLineSegment(sketch, "E119.2", {"start": v(-150, 30) * mm, "end": v(-150, 10) * mm});
            skLineSegment(sketch, "E119.3", {"start": v(-150, -50) * mm, "end": v(-150, -70) * mm});
            skLineSegment(sketch, "E119.4", {"start": v(-146, -70) * mm, "end": v(-150, -70) * mm});
            skLineSegment(sketch, "E119.5", {"start": v(-146, 70) * mm, "end": v(-150, 70) * mm});
            skLineSegment(sketch, "E119.6", {"start": v(-146, -50) * mm, "end": v(-150, -50) * mm});
            skLineSegment(sketch, "E119.7", {"start": v(-150, -90) * mm, "end": v(-150, -100) * mm});
            skLineSegment(sketch, "E119.8", {"start": v(-146, -10) * mm, "end": v(-150, -10) * mm});
            skLineSegment(sketch, "E119.9", {"start": v(-146, 30) * mm, "end": v(-150, 30) * mm});
            skLineSegment(sketch, "E119.11", {"start": v(-146, -30) * mm, "end": v(-150, -30) * mm});
            skLineSegment(sketch, "E119.12", {"start": v(-150, -50) * mm, "end": v(-150, -70) * mm});
            skLineSegment(sketch, "E119.13", {"start": v(-150, 100) * mm, "end": v(-150, 90) * mm});
            skLineSegment(sketch, "E119.14", {"start": v(-150, 70) * mm, "end": v(-150, 50) * mm});
            skLineSegment(sketch, "E119.15", {"start": v(-150, -10) * mm, "end": v(-150, -30) * mm});
            skLineSegment(sketch, "E119.16", {"start": v(-150, 100) * mm, "end": v(-150, 90) * mm});
            skLineSegment(sketch, "E119.17", {"start": v(-146, 90) * mm, "end": v(-150, 90) * mm});
            skLineSegment(sketch, "E119.18", {"start": v(-146, 10) * mm, "end": v(-146, -10) * mm});
            skLineSegment(sketch, "E119.19", {"start": v(-150, 70) * mm, "end": v(-150, 50) * mm});
            skLineSegment(sketch, "E119.20", {"start": v(-150, -10) * mm, "end": v(-150, -30) * mm});
            skLineSegment(sketch, "E119.21", {"start": v(-150, 30) * mm, "end": v(-150, 10) * mm});
            skLineSegment(sketch, "E119.22", {"start": v(-150, -70) * mm, "end": v(-150, -90) * mm});
            skLineSegment(sketch, "E119.23", {"start": v(-150, -90) * mm, "end": v(-150, -70) * mm});
            skLineSegment(sketch, "E119.24", {"start": v(-150, 50) * mm, "end": v(-150, 30) * mm});
            skLineSegment(sketch, "E119.25", {"start": v(-150, 30) * mm, "end": v(-150, 50) * mm});
            skLineSegment(sketch, "E119.26", {"start": v(-150, 90) * mm, "end": v(-150, 70) * mm});
            skLineSegment(sketch, "E119.27", {"start": v(-150, 70) * mm, "end": v(-150, 90) * mm});
            skLineSegment(sketch, "E119.28", {"start": v(-150, -30) * mm, "end": v(-150, -50) * mm});
            skLineSegment(sketch, "E119.29", {"start": v(-150, -50) * mm, "end": v(-150, -30) * mm});
            skLineSegment(sketch, "E119.30", {"start": v(-150, 10) * mm, "end": v(-150, -10) * mm});
            skLineSegment(sketch, "E119.31", {"start": v(-150, -10) * mm, "end": v(-150, 10) * mm});
            skLineSegment(sketch, "E119.33", {"start": v(-146, 70) * mm, "end": v(-150, 70) * mm});
            skLineSegment(sketch, "E119.34", {"start": v(-146, -50) * mm, "end": v(-150, -50) * mm});
            skLineSegment(sketch, "E119.35", {"start": v(-146, -30) * mm, "end": v(-150, -30) * mm});
            skLineSegment(sketch, "E119.38", {"start": v(-146, -50) * mm, "end": v(-146, -30) * mm});
            skLineSegment(sketch, "E119.40", {"start": v(-146, 70) * mm, "end": v(-146, 90) * mm});
            skLineSegment(sketch, "E119.41", {"start": v(-146, -90) * mm, "end": v(-146, -70) * mm});
            skLineSegment(sketch, "E119.43", {"start": v(-146, 30) * mm, "end": v(-146, 50) * mm});
            skLineSegment(sketch, "E119.45", {"start": v(-146, 30) * mm, "end": v(-146, 50) * mm});
            skLineSegment(sketch, "E119.48", {"start": v(-146, 50) * mm, "end": v(-150, 50) * mm});
            skLineSegment(sketch, "E119.51", {"start": v(-146, 10) * mm, "end": v(-150, 10) * mm});
            skLineSegment(sketch, "E119.55", {"start": v(-146, -90) * mm, "end": v(-146, -70) * mm});
            skLineSegment(sketch, "E119.56", {"start": v(-146, 70) * mm, "end": v(-146, 90) * mm});
            skLineSegment(sketch, "E119.57", {"start": v(-146, 10) * mm, "end": v(-146, -10) * mm});
            skLineSegment(sketch, "E119.59", {"start": v(-146, -50) * mm, "end": v(-146, -30) * mm});
            skLineSegment(sketch, "E119.61", {"start": v(-146, -70) * mm, "end": v(-150, -70) * mm});
            skLineSegment(sketch, "E119.62", {"start": v(-146, -90) * mm, "end": v(-150, -90) * mm});
            skLineSegment(sketch, "E119.63", {"start": v(-146, 30) * mm, "end": v(-150, 30) * mm});
            skLineSegment(sketch, "E119.64", {"start": v(-146, 70) * mm, "end": v(-150, 70) * mm});
            skLineSegment(sketch, "E119.65", {"start": v(-146, 90) * mm, "end": v(-150, 90) * mm});
            skLineSegment(sketch, "E119.66", {"start": v(-146, -50) * mm, "end": v(-150, -50) * mm});
            skLineSegment(sketch, "E119.67", {"start": v(-146, -30) * mm, "end": v(-150, -30) * mm});
            skLineSegment(sketch, "E119.68", {"start": v(-146, 10) * mm, "end": v(-146, -10) * mm});
            skLineSegment(sketch, "E119.69", {"start": v(-146, -10) * mm, "end": v(-150, -10) * mm});
            skLineSegment(sketch, "E119.70", {"start": v(-146, -70) * mm, "end": v(-150, -70) * mm});
            skLineSegment(sketch, "E119.71", {"start": v(-146, 50) * mm, "end": v(-150, 50) * mm});
            skLineSegment(sketch, "E119.74", {"start": v(-146, 30) * mm, "end": v(-150, 30) * mm});
            skLineSegment(sketch, "E119.77", {"start": v(-146, -10) * mm, "end": v(-150, -10) * mm});
            skLineSegment(sketch, "E119.79", {"start": v(-146, 90) * mm, "end": v(-150, 90) * mm});
            skLineSegment(sketch, "E119.83", {"start": v(-146, -70) * mm, "end": v(-146, -90) * mm});
            skLineSegment(sketch, "E119.84", {"start": v(-146, -90) * mm, "end": v(-146, -70) * mm});
            skLineSegment(sketch, "E119.85", {"start": v(-146, 50) * mm, "end": v(-150, 50) * mm});
            skLineSegment(sketch, "E119.87", {"start": v(-146, 50) * mm, "end": v(-146, 30) * mm});
            skLineSegment(sketch, "E119.89", {"start": v(-146, 30) * mm, "end": v(-146, 50) * mm});
            skLineSegment(sketch, "E119.90", {"start": v(-146, 70) * mm, "end": v(-146, 90) * mm});
            skLineSegment(sketch, "E119.91", {"start": v(-150, 70) * mm, "end": v(-146, 70) * mm});
            skLineSegment(sketch, "E119.94", {"start": v(-146, 90) * mm, "end": v(-146, 70) * mm});
            skLineSegment(sketch, "E119.96", {"start": v(-146, -50) * mm, "end": v(-146, -30) * mm});
            skLineSegment(sketch, "E119.98", {"start": v(-150, -30) * mm, "end": v(-146, -30) * mm});
            skLineSegment(sketch, "E119.99", {"start": v(-150, -50) * mm, "end": v(-146, -50) * mm});
            skLineSegment(sketch, "E119.100", {"start": v(-146, -30) * mm, "end": v(-146, -50) * mm});
            skLineSegment(sketch, "E119.101", {"start": v(-146, 10) * mm, "end": v(-150, 10) * mm});
            skLineSegment(sketch, "E119.104", {"start": v(-146, -10) * mm, "end": v(-146, 10) * mm});
            skLineSegment(sketch, "E119.105", {"start": v(-146, -90) * mm, "end": v(-150, -90) * mm});
            skLineSegment(sketch, "E119.106", {"start": v(-146, 10) * mm, "end": v(-150, 10) * mm});
            skLineSegment(sketch, "E119.109", {"start": v(-150, -70) * mm, "end": v(-146, -70) * mm});
            skLineSegment(sketch, "E119.110", {"start": v(-150, 50) * mm, "end": v(-146, 50) * mm});
            skLineSegment(sketch, "E119.113", {"start": v(-150, 30) * mm, "end": v(-146, 30) * mm});
            skLineSegment(sketch, "E119.116", {"start": v(-150, 90) * mm, "end": v(-146, 90) * mm});
            skLineSegment(sketch, "E119.121", {"start": v(-150, -10) * mm, "end": v(-146, -10) * mm});
            skLineSegment(sketch, "E119.122", {"start": v(-150, -90) * mm, "end": v(-146, -90) * mm});
            skLineSegment(sketch, "E119.123", {"start": v(-150, 10) * mm, "end": v(-146, 10) * mm});
            skLineSegment(sketch, "E120.bottom", {"start": v(-146, 100) * mm, "end": v(-150, 100) * mm});
            skLineSegment(sketch, "E120.top", {"start": v(-146, -100) * mm, "end": v(-150, -100) * mm});
            skLineSegment(sketch, "E120.left", {"start": v(-146, 100) * mm, "end": v(-146, -100) * mm});
            skLineSegment(sketch, "E120.right", {"start": v(-150, 100) * mm, "end": v(-150, -100) * mm});
            skSolve(sketch);
        }
        {
            var Q0;
            Q0 = qSketchRegion(id + "F9", true);
            extrude(context, id + "F10", {"entities" : qUnion([Q0]), "depth" : 100 * mm});
        }
        {
            var Q0;
            Q0=makeQuery(id+"F10.opExtrude","SWEPT_BODY",BODY,{"disambiguationData":[OSD([sQuery(id+"F9.wireOp",EDGE,"E120.bottom"),sQuery(id+"F9.wireOp",EDGE,"E120.top"),sQuery(id+"F9.wireOp",EDGE,"E120.left"),sQuery(id+"F9.wireOp",EDGE,"E120.right")])]});
            var Q1;
            Q1=makeQuery(id+"F8.opExtrude","SWEPT_BODY",BODY,{"disambiguationData":[OSD([sQuery(id+"F7.wireOp",EDGE,"E117.26"),sQuery(id+"F7.wireOp",EDGE,"E117.35"),sQuery(id+"F7.wireOp",EDGE,"E117.54"),sQuery(id+"F7.wireOp",EDGE,"E118")])]});
            var Q2;
            Q2=makeQuery(id+"F8.opExtrude","SWEPT_BODY",BODY,{"disambiguationData":[OSD([sQuery(id+"F7.wireOp",EDGE,"E117.24"),sQuery(id+"F7.wireOp",EDGE,"E117.38"),sQuery(id+"F7.wireOp",EDGE,"E117.40"),sQuery(id+"F7.wireOp",EDGE,"E118")])]});
            var Q3;
            Q3=makeQuery(id+"F8.opExtrude","SWEPT_BODY",BODY,{"disambiguationData":[OSD([sQuery(id+"F7.wireOp",EDGE,"E117.49"),sQuery(id+"F7.wireOp",EDGE,"E117.55"),sQuery(id+"F7.wireOp",EDGE,"E117.60"),sQuery(id+"F7.wireOp",EDGE,"E118")])]});
            var Q4;
            Q4=makeQuery(id+"F8.opExtrude","SWEPT_BODY",BODY,{"disambiguationData":[OSD([sQuery(id+"F7.wireOp",EDGE,"E117.27"),sQuery(id+"F7.wireOp",EDGE,"E117.29"),sQuery(id+"F7.wireOp",EDGE,"E117.61"),sQuery(id+"F7.wireOp",EDGE,"E118")])]});
            var Q5;
            Q5=makeQuery(id+"F8.opExtrude","SWEPT_BODY",BODY,{"disambiguationData":[OSD([sQuery(id+"F7.wireOp",EDGE,"E117.23"),sQuery(id+"F7.wireOp",EDGE,"E117.25"),sQuery(id+"F7.wireOp",EDGE,"E117.36"),sQuery(id+"F7.wireOp",EDGE,"E118")])]});
            booleanBodies(context, id + "F11", {"operationType" : BooleanOperationType.UNION, "tools" : qUnion([Q0, Q1, Q2, Q3, Q4, Q5])});
        }
        {
            var Q0;
            {var subQ0=sQuery(id+"F7.wireOp",EDGE,"E118");Q0=makeQuery(id+"F11.opBoolean","MERGE",FACE,{"derivedFrom":[makeQuery(id+"F8.opExtrude","SWEPT_FACE",FACE,{"disambiguationData":[OSD([subQ0]),TDD([makeQuery(id+"F7.imprint","IMPRINT",EDGE,{"disambiguationData":[TD([[makeQuery(id+"F7.imprint","INTERSECT",VERTEX,{"derivedFrom":[sQuery(id+"F7.wireOp",EDGE,"E117.54"),subQ0]}),-1.0]])],"derivedFrom":subQ0})])]}),makeQuery(id+"F8.opExtrude","SWEPT_FACE",FACE,{"disambiguationData":[OSD([subQ0]),TDD([makeQuery(id+"F7.imprint","IMPRINT",EDGE,{"disambiguationData":[TD([[makeQuery(id+"F7.imprint","INTERSECT",VERTEX,{"derivedFrom":[sQuery(id+"F7.wireOp",EDGE,"E117.38"),subQ0]}),1.0]])],"derivedFrom":subQ0})])]}),makeQuery(id+"F8.opExtrude","SWEPT_FACE",FACE,{"disambiguationData":[OSD([subQ0]),TDD([makeQuery(id+"F7.imprint","IMPRINT",EDGE,{"disambiguationData":[TD([[makeQuery(id+"F7.imprint","INTERSECT",VERTEX,{"derivedFrom":[sQuery(id+"F7.wireOp",EDGE,"E117.60"),subQ0]}),-1.0]])],"derivedFrom":subQ0})])]}),makeQuery(id+"F8.opExtrude","SWEPT_FACE",FACE,{"disambiguationData":[OSD([subQ0]),TDD([makeQuery(id+"F7.imprint","IMPRINT",EDGE,{"disambiguationData":[TD([[makeQuery(id+"F7.imprint","INTERSECT",VERTEX,{"derivedFrom":[sQuery(id+"F7.wireOp",EDGE,"E117.29"),subQ0]}),-1.0]])],"derivedFrom":subQ0})])]}),makeQuery(id+"F8.opExtrude","SWEPT_FACE",FACE,{"disambiguationData":[OSD([subQ0]),TDD([makeQuery(id+"F7.imprint","IMPRINT",EDGE,{"disambiguationData":[TD([[makeQuery(id+"F7.imprint","INTERSECT",VERTEX,{"derivedFrom":[sQuery(id+"F7.wireOp",EDGE,"E117.25"),subQ0]}),1.0]])],"derivedFrom":subQ0})])]}),makeQuery(id+"F10.opExtrude","SWEPT_FACE",FACE,{"disambiguationData":[OSD([sQuery(id+"F9.wireOp",EDGE,"E120.right")])]})]});}
            var sketch = newSketch(context, id + "F12", { "sketchPlane" : qUnion([Q0])});
            skLineSegment(sketch, "E121.bottom", {"start": v(-100, 4) * mm, "end": v(-96, 4) * mm});
            skLineSegment(sketch, "E121.top", {"start": v(-100, 24) * mm, "end": v(-96, 24) * mm});
            skLineSegment(sketch, "E121.left", {"start": v(-100, 4) * mm, "end": v(-100, 24) * mm});
            skLineSegment(sketch, "E121.right", {"start": v(-96, 4) * mm, "end": v(-96, 24) * mm});
            skLineSegment(sketch, "E122.0.1.0", {"start": v(-100, 44) * mm, "end": v(-96, 44) * mm});
            skLineSegment(sketch, "E122.0.1.1", {"start": v(-96, 44) * mm, "end": v(-96, 64) * mm});
            skLineSegment(sketch, "E122.0.1.2", {"start": v(-100, 64) * mm, "end": v(-96, 64) * mm});
            skLineSegment(sketch, "E122.0.2.0", {"start": v(-100, 84) * mm, "end": v(-96, 84) * mm});
            skLineSegment(sketch, "E122.0.2.1", {"start": v(-96, 84) * mm, "end": v(-96, 104) * mm});
            skLineSegment(sketch, "E122.0.2.2", {"start": v(-100, 104) * mm, "end": v(-96, 104) * mm});
            skLineSegment(sketch, "E122.direction1", {"start": v(-100, 4) * mm, "end": v(-75, 4) * mm, "construction": true});
            skLineSegment(sketch, "E122.direction2", {"start": v(-100, 4) * mm, "end": v(-100, 44) * mm, "construction": true});
            skLineSegment(sketch, "E123.MirrorCS", {"start": v(100, 4) * mm, "end": v(75, 4) * mm, "construction": true});
            skLineSegment(sketch, "E124.MirrorCS", {"start": v(100, 44) * mm, "end": v(96, 44) * mm});
            skLineSegment(sketch, "E125.MirrorCS", {"start": v(100, 24) * mm, "end": v(96, 24) * mm});
            skLineSegment(sketch, "E126.MirrorCS", {"start": v(100, 4) * mm, "end": v(96, 4) * mm});
            skLineSegment(sketch, "E127.MirrorCS", {"start": v(100, 104) * mm, "end": v(96, 104) * mm});
            skLineSegment(sketch, "E128.MirrorCS", {"start": v(100, 84) * mm, "end": v(96, 84) * mm});
            skLineSegment(sketch, "E129.MirrorCS", {"start": v(100, 64) * mm, "end": v(96, 64) * mm});
            skLineSegment(sketch, "E130.MirrorCS", {"start": v(100, 4) * mm, "end": v(100, 24) * mm});
            skLineSegment(sketch, "E131.MirrorCS", {"start": v(100, 4) * mm, "end": v(100, 44) * mm, "construction": true});
            skLineSegment(sketch, "E132.MirrorCS", {"start": v(96, 84) * mm, "end": v(96, 104) * mm});
            skLineSegment(sketch, "E133.MirrorCS", {"start": v(96, 44) * mm, "end": v(96, 64) * mm});
            skLineSegment(sketch, "E134.MirrorCS", {"start": v(96, 4) * mm, "end": v(96, 24) * mm});
            skSolve(sketch);
        }
        {
            var Q0;
            Q0=makeQuery(id+"F12.imprint","IMPRINT",FACE,{"disambiguationData":[TD([[makeQuery(id+"F12.imprint","IMPRINT",EDGE,{"derivedFrom":sQuery(id+"F12.wireOp",EDGE,"E121.bottom")}),1.0]])]});
            var Q1;
            {var subQ0=sQuery(id+"F12.wireOp",EDGE,"E122.0.1.0");Q1=makeQuery(id+"F12.imprint","IMPRINT",FACE,{"disambiguationData":[TD([[makeQuery(id+"F12.imprint","IMPRINT",EDGE,{"derivedFrom":subQ0}),1.0]])]});}
            var Q2;
            {var subQ0=sQuery(id+"F12.wireOp",EDGE,"E122.0.2.0");Q2=makeQuery(id+"F12.imprint","IMPRINT",FACE,{"disambiguationData":[TD([[makeQuery(id+"F12.imprint","IMPRINT",EDGE,{"derivedFrom":subQ0}),1.0]])]});}
            var Q3;
            Q3=makeQuery(id+"F12.imprint","IMPRINT",FACE,{"disambiguationData":[TD([[makeQuery(id+"F12.imprint","IMPRINT",EDGE,{"derivedFrom":sQuery(id+"F12.wireOp",EDGE,"E125.MirrorCS")}),1.0]])]});
            var Q4;
            {var subQ0=sQuery(id+"F12.wireOp",EDGE,"E124.MirrorCS");Q4=makeQuery(id+"F12.imprint","IMPRINT",FACE,{"disambiguationData":[TD([[makeQuery(id+"F12.imprint","IMPRINT",EDGE,{"derivedFrom":subQ0}),-1.0]])]});}
            var Q5;
            {var subQ0=sQuery(id+"F12.wireOp",EDGE,"E127.MirrorCS");Q5=makeQuery(id+"F12.imprint","IMPRINT",FACE,{"disambiguationData":[TD([[makeQuery(id+"F12.imprint","IMPRINT",EDGE,{"derivedFrom":subQ0}),-1.0]])]});}
            var Q6;
            Q6=makeQuery(id+"F11.opBoolean","MERGE",FACE,{"derivedFrom":[makeQuery(id+"F8.opExtrude","SWEPT_FACE",FACE,{"disambiguationData":[OSD([sQuery(id+"F7.wireOp",EDGE,"E117.35")])]}),makeQuery(id+"F8.opExtrude","SWEPT_FACE",FACE,{"disambiguationData":[OSD([sQuery(id+"F7.wireOp",EDGE,"E117.36")])]}),makeQuery(id+"F8.opExtrude","SWEPT_FACE",FACE,{"disambiguationData":[OSD([sQuery(id+"F7.wireOp",EDGE,"E117.40")])]}),makeQuery(id+"F8.opExtrude","SWEPT_FACE",FACE,{"disambiguationData":[OSD([sQuery(id+"F7.wireOp",EDGE,"E117.55")])]}),makeQuery(id+"F8.opExtrude","SWEPT_FACE",FACE,{"disambiguationData":[OSD([sQuery(id+"F7.wireOp",EDGE,"E117.61")])]}),makeQuery(id+"F10.opExtrude","SWEPT_FACE",FACE,{"disambiguationData":[OSD([sQuery(id+"F9.wireOp",EDGE,"E120.left")])]})]});
            extrude(context, id + "F13", {"entities" : qUnion([Q0, Q1, Q2, Q3, Q4, Q5]), "operationType" : NewBodyOperationType.REMOVE, "endBound" : BoundingType.UP_TO_SURFACE, "oppositeDirection" : true, "endBoundEntityFace" : qUnion([Q6]), "depth" : 25 * mm});
        }
        {
            var Q0;
            {var subQ0=sQuery(id+"F2.wireOp",EDGE,"E114");Q0=makeQuery(id+"F6.opBoolean","MERGE",FACE,{"derivedFrom":[makeQuery(id+"F3.opExtrude","SWEPT_FACE",FACE,{"disambiguationData":[OSD([subQ0]),TDD([makeQuery(id+"F2.imprint","IMPRINT",EDGE,{"disambiguationData":[TD([[makeQuery(id+"F2.imprint","INTERSECT",VERTEX,{"derivedFrom":[sQuery(id+"F2.wireOp",EDGE,"E113.49"),subQ0]}),1.0],[makeQuery(id+"F2.imprint","INTERSECT",VERTEX,{"derivedFrom":[sQuery(id+"F2.wireOp",EDGE,"E113.46"),subQ0]}),-1.0]])],"derivedFrom":subQ0})])]}),makeQuery(id+"F3.opExtrude","SWEPT_FACE",FACE,{"disambiguationData":[OSD([subQ0]),TDD([makeQuery(id+"F2.imprint","IMPRINT",EDGE,{"disambiguationData":[TD([[makeQuery(id+"F2.imprint","INTERSECT",VERTEX,{"derivedFrom":[sQuery(id+"F2.wireOp",EDGE,"E113.54"),subQ0]}),1.0],[makeQuery(id+"F2.imprint","INTERSECT",VERTEX,{"derivedFrom":[sQuery(id+"F2.wireOp",EDGE,"E113.85"),subQ0]}),-1.0]])],"derivedFrom":subQ0})])]}),makeQuery(id+"F3.opExtrude","SWEPT_FACE",FACE,{"disambiguationData":[OSD([subQ0]),TDD([makeQuery(id+"F2.imprint","IMPRINT",EDGE,{"disambiguationData":[TD([[makeQuery(id+"F2.imprint","INTERSECT",VERTEX,{"derivedFrom":[sQuery(id+"F2.wireOp",EDGE,"E113.42"),subQ0]}),-1.0],[makeQuery(id+"F2.imprint","INTERSECT",VERTEX,{"derivedFrom":[sQuery(id+"F2.wireOp",EDGE,"E113.67"),subQ0]}),1.0]])],"derivedFrom":subQ0})])]}),makeQuery(id+"F3.opExtrude","SWEPT_FACE",FACE,{"disambiguationData":[OSD([subQ0]),TDD([makeQuery(id+"F2.imprint","IMPRINT",EDGE,{"disambiguationData":[TD([[makeQuery(id+"F2.imprint","INTERSECT",VERTEX,{"derivedFrom":[sQuery(id+"F2.wireOp",EDGE,"E113.56"),subQ0]}),1.0],[makeQuery(id+"F2.imprint","INTERSECT",VERTEX,{"derivedFrom":[sQuery(id+"F2.wireOp",EDGE,"E113.80"),subQ0]}),-1.0]])],"derivedFrom":subQ0})])]}),makeQuery(id+"F3.opExtrude","SWEPT_FACE",FACE,{"disambiguationData":[OSD([subQ0]),TDD([makeQuery(id+"F2.imprint","IMPRINT",EDGE,{"disambiguationData":[TD([[makeQuery(id+"F2.imprint","INTERSECT",VERTEX,{"derivedFrom":[sQuery(id+"F2.wireOp",EDGE,"E113.83"),subQ0]}),-1.0],[makeQuery(id+"F2.imprint","INTERSECT",VERTEX,{"derivedFrom":[sQuery(id+"F2.wireOp",EDGE,"E113.57"),subQ0]}),1.0]])],"derivedFrom":subQ0})])]}),makeQuery(id+"F3.opExtrude","SWEPT_FACE",FACE,{"disambiguationData":[OSD([subQ0]),TDD([makeQuery(id+"F2.imprint","IMPRINT",EDGE,{"disambiguationData":[TD([[makeQuery(id+"F2.imprint","INTERSECT",VERTEX,{"derivedFrom":[sQuery(id+"F2.wireOp",EDGE,"E113.63"),subQ0]}),-1.0],[makeQuery(id+"F2.imprint","INTERSECT",VERTEX,{"derivedFrom":[sQuery(id+"F2.wireOp",EDGE,"E113.69"),subQ0]}),1.0]])],"derivedFrom":subQ0})])]}),makeQuery(id+"F3.opExtrude","SWEPT_FACE",FACE,{"disambiguationData":[OSD([subQ0]),TDD([makeQuery(id+"F2.imprint","IMPRINT",EDGE,{"disambiguationData":[TD([[makeQuery(id+"F2.imprint","INTERSECT",VERTEX,{"derivedFrom":[sQuery(id+"F2.wireOp",EDGE,"E113.84"),subQ0]}),1.0],[makeQuery(id+"F2.imprint","INTERSECT",VERTEX,{"derivedFrom":[sQuery(id+"F2.wireOp",EDGE,"E113.55"),subQ0]}),-1.0]])],"derivedFrom":subQ0})])]}),makeQuery(id+"F5.opExtrude","SWEPT_FACE",FACE,{"disambiguationData":[OSD([sQuery(id+"F4.wireOp",EDGE,"E116.top")])]})]});}
            var sketch = newSketch(context, id + "F14", { "sketchPlane" : qUnion([Q0])});
            skLineSegment(sketch, "E135.0.0", {"start": v(150, 84) * mm, "end": v(146, 84) * mm});
            skLineSegment(sketch, "E135.0.1", {"start": v(146, 84) * mm, "end": v(146, 64) * mm});
            skLineSegment(sketch, "E135.0.2", {"start": v(146, 64) * mm, "end": v(150, 64) * mm});
            skLineSegment(sketch, "E135.0.3", {"start": v(150, 64) * mm, "end": v(150, 84) * mm});
            skLineSegment(sketch, "E136.0", {"start": v(146, 44) * mm, "end": v(146, 24) * mm});
            skLineSegment(sketch, "E137.0.1", {"start": v(146, 24) * mm, "end": v(150, 24) * mm});
            skLineSegment(sketch, "E137.0.2", {"start": v(150, 24) * mm, "end": v(150, 44) * mm});
            skLineSegment(sketch, "E137.0.3", {"start": v(150, 44) * mm, "end": v(146, 44) * mm});
            skLineSegment(sketch, "E138.MirrorCS", {"start": v(-146, 44) * mm, "end": v(-146, 24) * mm});
            skLineSegment(sketch, "E139.MirrorCS", {"start": v(-150, 44) * mm, "end": v(-146, 44) * mm});
            skLineSegment(sketch, "E140.MirrorCS", {"start": v(-150, 24) * mm, "end": v(-150, 44) * mm});
            skLineSegment(sketch, "E141.MirrorCS", {"start": v(-146, 24) * mm, "end": v(-150, 24) * mm});
            skLineSegment(sketch, "E142.MirrorCS", {"start": v(-150, 84) * mm, "end": v(-146, 84) * mm});
            skLineSegment(sketch, "E143.MirrorCS", {"start": v(-146, 64) * mm, "end": v(-150, 64) * mm});
            skLineSegment(sketch, "E144.MirrorCS", {"start": v(-150, 64) * mm, "end": v(-150, 84) * mm});
            skLineSegment(sketch, "E145.MirrorCS", {"start": v(-146, 84) * mm, "end": v(-146, 64) * mm});
            skSolve(sketch);
        }
        {
            var Q0;
            Q0=makeQuery(id+"F14.imprint","IMPRINT",FACE,{"disambiguationData":[TD([[makeQuery(id+"F14.imprint","IMPRINT",EDGE,{"derivedFrom":sQuery(id+"F14.wireOp",EDGE,"E142.MirrorCS")}),-1.0]])]});
            var Q1;
            Q1=makeQuery(id+"F14.imprint","IMPRINT",FACE,{"disambiguationData":[TD([[makeQuery(id+"F14.imprint","IMPRINT",EDGE,{"derivedFrom":sQuery(id+"F14.wireOp",EDGE,"E141.MirrorCS")}),-1.0]])]});
            var Q2;
            Q2=makeQuery(id+"F14.imprint","IMPRINT",FACE,{"disambiguationData":[TD([[makeQuery(id+"F14.imprint","IMPRINT",EDGE,{"derivedFrom":sQuery(id+"F14.wireOp",EDGE,"E135.0.0")}),1.0]])]});
            var Q3;
            Q3=makeQuery(id+"F14.imprint","IMPRINT",FACE,{"disambiguationData":[TD([[makeQuery(id+"F14.imprint","IMPRINT",EDGE,{"derivedFrom":sQuery(id+"F14.wireOp",EDGE,"E136.0")}),1.0]])]});
            var Q4;
            Q4=makeQuery(id+"F6.opBoolean","MERGE",FACE,{"derivedFrom":[makeQuery(id+"F3.opExtrude","SWEPT_FACE",FACE,{"disambiguationData":[OSD([sQuery(id+"F2.wireOp",EDGE,"E113.37")])]}),makeQuery(id+"F3.opExtrude","SWEPT_FACE",FACE,{"disambiguationData":[OSD([sQuery(id+"F2.wireOp",EDGE,"E113.38")])]}),makeQuery(id+"F3.opExtrude","SWEPT_FACE",FACE,{"disambiguationData":[OSD([sQuery(id+"F2.wireOp",EDGE,"E113.47")])]}),makeQuery(id+"F3.opExtrude","SWEPT_FACE",FACE,{"disambiguationData":[OSD([sQuery(id+"F2.wireOp",EDGE,"E113.62")])]}),makeQuery(id+"F3.opExtrude","SWEPT_FACE",FACE,{"disambiguationData":[OSD([sQuery(id+"F2.wireOp",EDGE,"E113.70")])]}),makeQuery(id+"F3.opExtrude","SWEPT_FACE",FACE,{"disambiguationData":[OSD([sQuery(id+"F2.wireOp",EDGE,"E113.76")])]}),makeQuery(id+"F3.opExtrude","SWEPT_FACE",FACE,{"disambiguationData":[OSD([sQuery(id+"F2.wireOp",EDGE,"E113.79")])]}),makeQuery(id+"F5.opExtrude","SWEPT_FACE",FACE,{"disambiguationData":[OSD([sQuery(id+"F4.wireOp",EDGE,"E116.bottom")])]})]});
            extrude(context, id + "F15", {"entities" : qUnion([Q0, Q1, Q2, Q3]), "operationType" : NewBodyOperationType.REMOVE, "endBound" : BoundingType.UP_TO_SURFACE, "oppositeDirection" : true, "endBoundEntityFace" : qUnion([Q4]), "depth" : 25 * mm});
        }
    });
